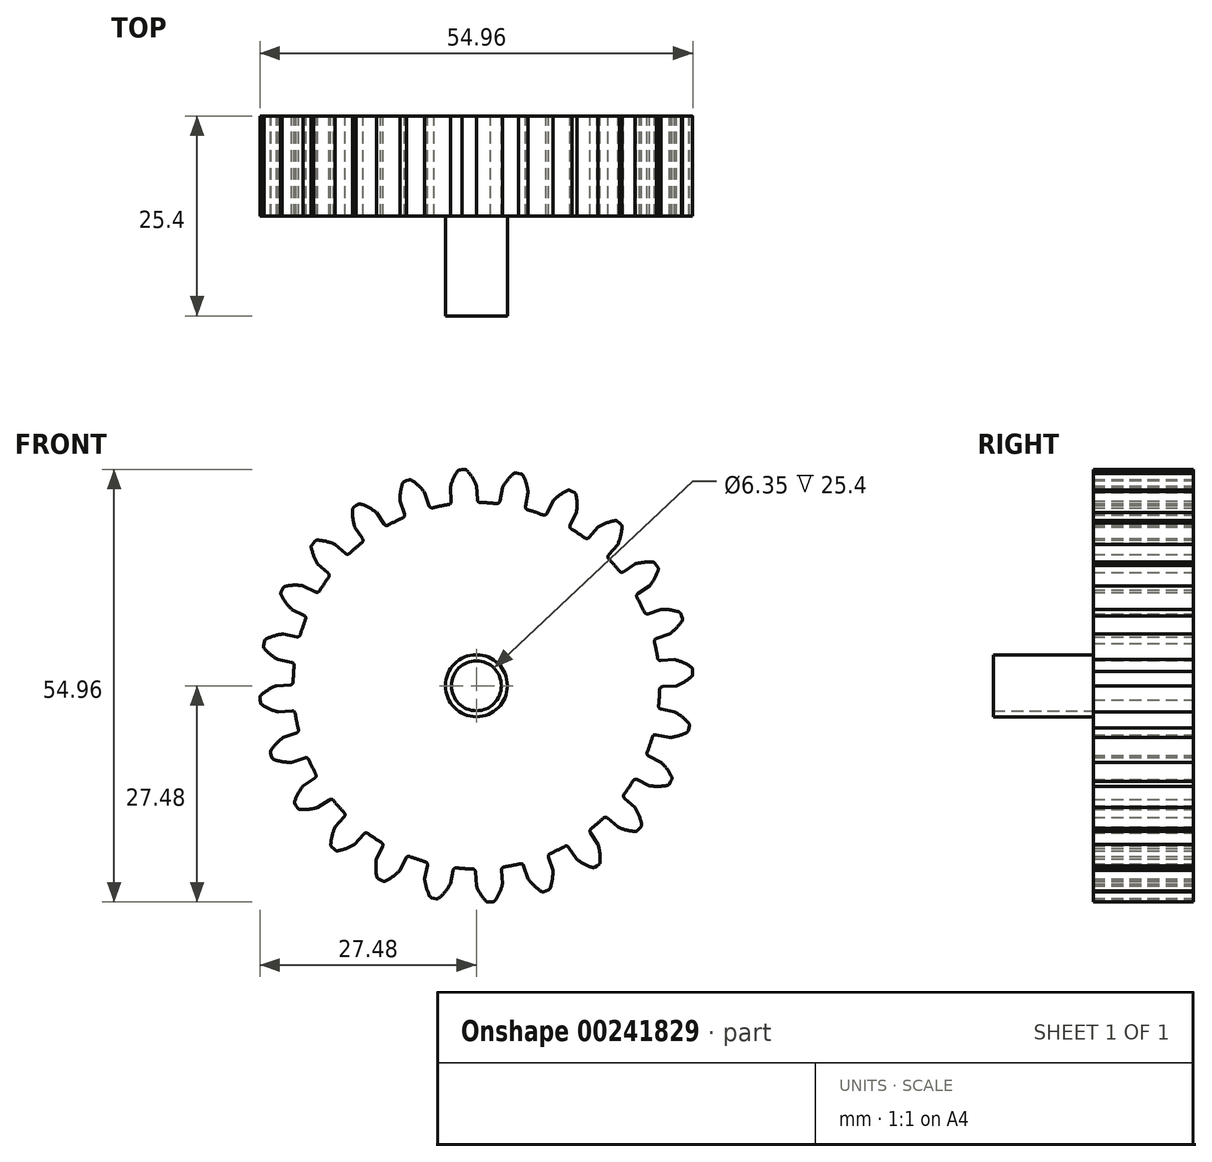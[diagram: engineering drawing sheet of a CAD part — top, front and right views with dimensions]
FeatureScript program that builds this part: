
annotation { "Feature Type Name" : "Feature", "Feature Type Description" : "" }
export const myFeature = defineFeature(function(context is Context, id is Id, definition is map)
    precondition{}
    {
        {
            var Q0;
            Q0=qCreatedBy(makeId("Front.planeOp"),FACE);
            var sketch = newSketch(context, id + "F0", { "sketchPlane" : qUnion([Q0])});
            skArc(sketch, "E0", {"start": v(-3.52, 23.02) * mm, "mid": v(-4.54, 22.84) * mm, "end": v(-5.55, 22.61) * mm});
            skArc(sketch, "E1.trimOffspring", {"start": v(0, 25.4) * mm, "mid": v(-0.5, 26.43) * mm, "end": v(-1.2, 27.35) * mm});
            skLineSegment(sketch, "E2", {"start": v(0, 25.4) * mm, "end": v(0.12, 23.63) * mm});
            skLineSegment(sketch, "E3", {"start": v(-1.5, 27.48) * mm, "end": v(-1.8, 27.46) * mm});
            skLineSegment(sketch, "E4.MirrorCS", {"start": v(-2.1, 27.44) * mm, "end": v(-1.8, 27.46) * mm});
            skArc(sketch, "E5.MirrorCS", {"start": v(-3.32, 25.18) * mm, "mid": v(-2.95, 26.27) * mm, "end": v(-2.39, 27.27) * mm});
            skLineSegment(sketch, "E6.MirrorCS", {"start": v(-3.32, 25.18) * mm, "end": v(-3.2, 23.42) * mm});
            skPoint(sketch, "E7.visualSharp", {"position": v(-2.28, 27.42) * mm});
            skArc(sketch, "E7.filletArc", {"start": v(-2.1, 27.44) * mm, "mid": v(-2.27, 27.39) * mm, "end": v(-2.39, 27.27) * mm});
            skPoint(sketch, "E8.visualSharp", {"position": v(-1.31, 27.49) * mm});
            skArc(sketch, "E8.filletArc", {"start": v(-1.2, 27.35) * mm, "mid": v(-1.33, 27.45) * mm, "end": v(-1.5, 27.48) * mm});
            skPoint(sketch, "E9.visualSharp", {"position": v(0.14, 23.28) * mm});
            skArc(sketch, "E9.filletArc", {"start": v(0.12, 23.63) * mm, "mid": v(0.23, 23.38) * mm, "end": v(0.49, 23.28) * mm});
            skPoint(sketch, "E10.visualSharp", {"position": v(-3.18, 23.07) * mm});
            skArc(sketch, "E10.filletArc", {"start": v(-3.52, 23.02) * mm, "mid": v(-3.28, 23.15) * mm, "end": v(-3.2, 23.42) * mm});
            skPoint(sketch, "E11.1.0", {"position": v(-8.38, 26.2) * mm});
            skPoint(sketch, "E11.1.1", {"position": v(-9.04, 21.46) * mm});
            skArc(sketch, "E11.1.2", {"start": v(-6.57, 24.53) * mm, "mid": v(-7.33, 25.4) * mm, "end": v(-8.23, 26.1) * mm});
            skArc(sketch, "E11.1.3", {"start": v(-9.72, 23.47) * mm, "mid": v(-9.65, 24.61) * mm, "end": v(-9.37, 25.72) * mm});
            skLineSegment(sketch, "E11.1.4", {"start": v(-9.72, 23.47) * mm, "end": v(-9.15, 21.8) * mm});
            skPoint(sketch, "E11.1.5", {"position": v(-9.3, 25.9) * mm});
            skLineSegment(sketch, "E11.1.6", {"start": v(-6.57, 24.53) * mm, "end": v(-6, 22.86) * mm});
            skLineSegment(sketch, "E11.1.7", {"start": v(-9.14, 25.96) * mm, "end": v(-8.85, 26.06) * mm});
            skArc(sketch, "E11.1.8", {"start": v(-9.14, 25.96) * mm, "mid": v(-9.28, 25.87) * mm, "end": v(-9.37, 25.72) * mm});
            skArc(sketch, "E11.1.9", {"start": v(-8.23, 26.1) * mm, "mid": v(-8.39, 26.17) * mm, "end": v(-8.55, 26.15) * mm});
            skLineSegment(sketch, "E11.1.10", {"start": v(-8.55, 26.15) * mm, "end": v(-8.85, 26.06) * mm});
            skArc(sketch, "E11.1.11", {"start": v(-6, 22.86) * mm, "mid": v(-5.83, 22.65) * mm, "end": v(-5.55, 22.61) * mm});
            skArc(sketch, "E11.1.12", {"start": v(-9.36, 21.32) * mm, "mid": v(-9.16, 21.51) * mm, "end": v(-9.15, 21.8) * mm});
            skPoint(sketch, "E11.2.0", {"position": v(-14.88, 23.15) * mm});
            skPoint(sketch, "E11.2.1", {"position": v(-14.28, 18.39) * mm});
            skArc(sketch, "E11.2.2", {"start": v(-12.7, 22) * mm, "mid": v(-13.65, 22.63) * mm, "end": v(-14.7, 23.1) * mm});
            skArc(sketch, "E11.2.3", {"start": v(-15.46, 20.15) * mm, "mid": v(-15.69, 21.28) * mm, "end": v(-15.7, 22.42) * mm});
            skLineSegment(sketch, "E11.2.4", {"start": v(-15.46, 20.15) * mm, "end": v(-14.48, 18.68) * mm});
            skPoint(sketch, "E11.2.5", {"position": v(-15.69, 22.6) * mm});
            skLineSegment(sketch, "E11.2.6", {"start": v(-12.7, 22) * mm, "end": v(-11.72, 20.53) * mm});
            skLineSegment(sketch, "E11.2.7", {"start": v(-15.54, 22.7) * mm, "end": v(-15.29, 22.88) * mm});
            skArc(sketch, "E11.2.8", {"start": v(-15.54, 22.7) * mm, "mid": v(-15.66, 22.58) * mm, "end": v(-15.7, 22.42) * mm});
            skArc(sketch, "E11.2.9", {"start": v(-14.7, 23.1) * mm, "mid": v(-14.87, 23.1) * mm, "end": v(-15.03, 23.05) * mm});
            skLineSegment(sketch, "E11.2.10", {"start": v(-15.03, 23.05) * mm, "end": v(-15.29, 22.88) * mm});
            skArc(sketch, "E11.2.11", {"start": v(-11.72, 20.53) * mm, "mid": v(-11.5, 20.37) * mm, "end": v(-11.22, 20.4) * mm});
            skArc(sketch, "E11.2.12", {"start": v(-14.56, 18.17) * mm, "mid": v(-14.42, 18.41) * mm, "end": v(-14.48, 18.68) * mm});
            skPoint(sketch, "E11.3.0", {"position": v(-20.36, 18.5) * mm});
            skPoint(sketch, "E11.3.1", {"position": v(-18.56, 14.06) * mm});
            skArc(sketch, "E11.3.2", {"start": v(-17.96, 17.96) * mm, "mid": v(-19.05, 18.33) * mm, "end": v(-20.18, 18.5) * mm});
            skArc(sketch, "E11.3.3", {"start": v(-20.15, 15.46) * mm, "mid": v(-20.66, 16.5) * mm, "end": v(-20.97, 17.6) * mm});
            skLineSegment(sketch, "E11.3.4", {"start": v(-20.15, 15.46) * mm, "end": v(-18.82, 14.3) * mm});
            skPoint(sketch, "E11.3.5", {"position": v(-21, 17.77) * mm});
            skLineSegment(sketch, "E11.3.6", {"start": v(-17.96, 17.96) * mm, "end": v(-16.63, 16.8) * mm});
            skLineSegment(sketch, "E11.3.7", {"start": v(-20.9, 17.91) * mm, "end": v(-20.7, 18.15) * mm});
            skArc(sketch, "E11.3.8", {"start": v(-20.9, 17.91) * mm, "mid": v(-20.97, 17.76) * mm, "end": v(-20.97, 17.6) * mm});
            skArc(sketch, "E11.3.9", {"start": v(-20.18, 18.5) * mm, "mid": v(-20.35, 18.47) * mm, "end": v(-20.48, 18.37) * mm});
            skLineSegment(sketch, "E11.3.10", {"start": v(-20.48, 18.37) * mm, "end": v(-20.7, 18.15) * mm});
            skArc(sketch, "E11.3.11", {"start": v(-16.63, 16.8) * mm, "mid": v(-16.37, 16.7) * mm, "end": v(-16.12, 16.8) * mm});
            skArc(sketch, "E11.3.12", {"start": v(-18.76, 13.78) * mm, "mid": v(-18.7, 14.05) * mm, "end": v(-18.82, 14.3) * mm});
            skPoint(sketch, "E11.4.0", {"position": v(-24.46, 12.6) * mm});
            skPoint(sketch, "E11.4.1", {"position": v(-21.56, 8.78) * mm});
            skArc(sketch, "E11.4.2", {"start": v(-22, 12.7) * mm, "mid": v(-23.14, 12.78) * mm, "end": v(-24.28, 12.64) * mm});
            skArc(sketch, "E11.4.3", {"start": v(-23.47, 9.72) * mm, "mid": v(-24.22, 10.58) * mm, "end": v(-24.81, 11.57) * mm});
            skLineSegment(sketch, "E11.4.4", {"start": v(-23.47, 9.72) * mm, "end": v(-21.88, 8.94) * mm});
            skPoint(sketch, "E11.4.5", {"position": v(-24.89, 11.73) * mm});
            skLineSegment(sketch, "E11.4.6", {"start": v(-22, 12.7) * mm, "end": v(-20.4, 11.92) * mm});
            skLineSegment(sketch, "E11.4.7", {"start": v(-24.81, 11.9) * mm, "end": v(-24.68, 12.17) * mm});
            skArc(sketch, "E11.4.8", {"start": v(-24.81, 11.9) * mm, "mid": v(-24.85, 11.73) * mm, "end": v(-24.81, 11.57) * mm});
            skArc(sketch, "E11.4.9", {"start": v(-24.28, 12.64) * mm, "mid": v(-24.43, 12.57) * mm, "end": v(-24.54, 12.45) * mm});
            skLineSegment(sketch, "E11.4.10", {"start": v(-24.54, 12.45) * mm, "end": v(-24.68, 12.17) * mm});
            skArc(sketch, "E11.4.11", {"start": v(-20.4, 11.92) * mm, "mid": v(-20.13, 11.9) * mm, "end": v(-19.92, 12.06) * mm});
            skArc(sketch, "E11.4.12", {"start": v(-21.7, 8.46) * mm, "mid": v(-21.7, 8.73) * mm, "end": v(-21.88, 8.94) * mm});
            skPoint(sketch, "E11.5.0", {"position": v(-26.89, 5.84) * mm});
            skPoint(sketch, "E11.5.1", {"position": v(-23.1, 2.9) * mm});
            skArc(sketch, "E11.5.2", {"start": v(-24.53, 6.57) * mm, "mid": v(-25.66, 6.35) * mm, "end": v(-26.73, 5.93) * mm});
            skArc(sketch, "E11.5.3", {"start": v(-25.18, 3.32) * mm, "mid": v(-26.14, 3.95) * mm, "end": v(-26.96, 4.75) * mm});
            skLineSegment(sketch, "E11.5.4", {"start": v(-25.18, 3.32) * mm, "end": v(-23.45, 2.97) * mm});
            skPoint(sketch, "E11.5.5", {"position": v(-27.08, 4.9) * mm});
            skLineSegment(sketch, "E11.5.6", {"start": v(-24.53, 6.57) * mm, "end": v(-22.8, 6.23) * mm});
            skLineSegment(sketch, "E11.5.7", {"start": v(-27.05, 5.07) * mm, "end": v(-27, 5.37) * mm});
            skArc(sketch, "E11.5.8", {"start": v(-27.05, 5.07) * mm, "mid": v(-27.04, 4.9) * mm, "end": v(-26.96, 4.75) * mm});
            skArc(sketch, "E11.5.9", {"start": v(-26.73, 5.93) * mm, "mid": v(-26.86, 5.82) * mm, "end": v(-26.93, 5.67) * mm});
            skLineSegment(sketch, "E11.5.10", {"start": v(-26.93, 5.67) * mm, "end": v(-27, 5.37) * mm});
            skArc(sketch, "E11.5.11", {"start": v(-22.8, 6.23) * mm, "mid": v(-22.53, 6.28) * mm, "end": v(-22.36, 6.5) * mm});
            skArc(sketch, "E11.5.12", {"start": v(-23.14, 2.55) * mm, "mid": v(-23.21, 2.82) * mm, "end": v(-23.45, 2.97) * mm});
            skPoint(sketch, "E11.6.0", {"position": v(-27.49, -1.31) * mm});
            skPoint(sketch, "E11.6.1", {"position": v(-23.07, -3.18) * mm});
            skArc(sketch, "E11.6.2", {"start": v(-25.4, 0) * mm, "mid": v(-26.43, -0.5) * mm, "end": v(-27.35, -1.2) * mm});
            skArc(sketch, "E11.6.3", {"start": v(-25.18, -3.32) * mm, "mid": v(-26.27, -2.95) * mm, "end": v(-27.27, -2.39) * mm});
            skLineSegment(sketch, "E11.6.4", {"start": v(-25.18, -3.32) * mm, "end": v(-23.42, -3.2) * mm});
            skPoint(sketch, "E11.6.5", {"position": v(-27.42, -2.28) * mm});
            skLineSegment(sketch, "E11.6.6", {"start": v(-25.4, 0) * mm, "end": v(-23.63, 0.12) * mm});
            skLineSegment(sketch, "E11.6.7", {"start": v(-27.44, -2.1) * mm, "end": v(-27.46, -1.8) * mm});
            skArc(sketch, "E11.6.8", {"start": v(-27.44, -2.1) * mm, "mid": v(-27.39, -2.27) * mm, "end": v(-27.27, -2.39) * mm});
            skArc(sketch, "E11.6.9", {"start": v(-27.35, -1.2) * mm, "mid": v(-27.45, -1.33) * mm, "end": v(-27.48, -1.5) * mm});
            skLineSegment(sketch, "E11.6.10", {"start": v(-27.48, -1.5) * mm, "end": v(-27.46, -1.8) * mm});
            skArc(sketch, "E11.6.11", {"start": v(-23.63, 0.12) * mm, "mid": v(-23.38, 0.23) * mm, "end": v(-23.28, 0.49) * mm});
            skArc(sketch, "E11.6.12", {"start": v(-23.02, -3.52) * mm, "mid": v(-23.15, -3.28) * mm, "end": v(-23.42, -3.2) * mm});
            skPoint(sketch, "E11.7.0", {"position": v(-26.2, -8.38) * mm});
            skPoint(sketch, "E11.7.1", {"position": v(-21.46, -9.04) * mm});
            skArc(sketch, "E11.7.2", {"start": v(-24.53, -6.57) * mm, "mid": v(-25.4, -7.33) * mm, "end": v(-26.1, -8.23) * mm});
            skArc(sketch, "E11.7.3", {"start": v(-23.47, -9.72) * mm, "mid": v(-24.61, -9.65) * mm, "end": v(-25.72, -9.37) * mm});
            skLineSegment(sketch, "E11.7.4", {"start": v(-23.47, -9.72) * mm, "end": v(-21.8, -9.15) * mm});
            skPoint(sketch, "E11.7.5", {"position": v(-25.9, -9.3) * mm});
            skLineSegment(sketch, "E11.7.6", {"start": v(-24.53, -6.57) * mm, "end": v(-22.86, -6) * mm});
            skLineSegment(sketch, "E11.7.7", {"start": v(-25.96, -9.14) * mm, "end": v(-26.06, -8.85) * mm});
            skArc(sketch, "E11.7.8", {"start": v(-25.96, -9.14) * mm, "mid": v(-25.87, -9.28) * mm, "end": v(-25.72, -9.37) * mm});
            skArc(sketch, "E11.7.9", {"start": v(-26.1, -8.23) * mm, "mid": v(-26.17, -8.39) * mm, "end": v(-26.15, -8.55) * mm});
            skLineSegment(sketch, "E11.7.10", {"start": v(-26.15, -8.55) * mm, "end": v(-26.06, -8.85) * mm});
            skArc(sketch, "E11.7.11", {"start": v(-22.86, -6) * mm, "mid": v(-22.65, -5.83) * mm, "end": v(-22.61, -5.55) * mm});
            skArc(sketch, "E11.7.12", {"start": v(-21.32, -9.36) * mm, "mid": v(-21.51, -9.16) * mm, "end": v(-21.8, -9.15) * mm});
            skPoint(sketch, "E11.8.0", {"position": v(-23.15, -14.88) * mm});
            skPoint(sketch, "E11.8.1", {"position": v(-18.39, -14.28) * mm});
            skArc(sketch, "E11.8.2", {"start": v(-22, -12.7) * mm, "mid": v(-22.63, -13.65) * mm, "end": v(-23.1, -14.7) * mm});
            skArc(sketch, "E11.8.3", {"start": v(-20.15, -15.46) * mm, "mid": v(-21.28, -15.69) * mm, "end": v(-22.42, -15.7) * mm});
            skLineSegment(sketch, "E11.8.4", {"start": v(-20.15, -15.46) * mm, "end": v(-18.68, -14.48) * mm});
            skPoint(sketch, "E11.8.5", {"position": v(-22.6, -15.69) * mm});
            skLineSegment(sketch, "E11.8.6", {"start": v(-22, -12.7) * mm, "end": v(-20.53, -11.72) * mm});
            skLineSegment(sketch, "E11.8.7", {"start": v(-22.7, -15.54) * mm, "end": v(-22.88, -15.29) * mm});
            skArc(sketch, "E11.8.8", {"start": v(-22.7, -15.54) * mm, "mid": v(-22.58, -15.66) * mm, "end": v(-22.42, -15.7) * mm});
            skArc(sketch, "E11.8.9", {"start": v(-23.1, -14.7) * mm, "mid": v(-23.1, -14.87) * mm, "end": v(-23.05, -15.03) * mm});
            skLineSegment(sketch, "E11.8.10", {"start": v(-23.05, -15.03) * mm, "end": v(-22.88, -15.29) * mm});
            skArc(sketch, "E11.8.11", {"start": v(-20.53, -11.72) * mm, "mid": v(-20.37, -11.5) * mm, "end": v(-20.4, -11.22) * mm});
            skArc(sketch, "E11.8.12", {"start": v(-18.17, -14.56) * mm, "mid": v(-18.41, -14.42) * mm, "end": v(-18.68, -14.48) * mm});
            skPoint(sketch, "E11.9.0", {"position": v(-18.5, -20.36) * mm});
            skPoint(sketch, "E11.9.1", {"position": v(-14.06, -18.56) * mm});
            skArc(sketch, "E11.9.2", {"start": v(-17.96, -17.96) * mm, "mid": v(-18.33, -19.05) * mm, "end": v(-18.5, -20.18) * mm});
            skArc(sketch, "E11.9.3", {"start": v(-15.46, -20.15) * mm, "mid": v(-16.5, -20.66) * mm, "end": v(-17.6, -20.97) * mm});
            skLineSegment(sketch, "E11.9.4", {"start": v(-15.46, -20.15) * mm, "end": v(-14.3, -18.82) * mm});
            skPoint(sketch, "E11.9.5", {"position": v(-17.77, -21) * mm});
            skLineSegment(sketch, "E11.9.6", {"start": v(-17.96, -17.96) * mm, "end": v(-16.8, -16.63) * mm});
            skLineSegment(sketch, "E11.9.7", {"start": v(-17.91, -20.9) * mm, "end": v(-18.15, -20.7) * mm});
            skArc(sketch, "E11.9.8", {"start": v(-17.91, -20.9) * mm, "mid": v(-17.76, -20.97) * mm, "end": v(-17.6, -20.97) * mm});
            skArc(sketch, "E11.9.9", {"start": v(-18.5, -20.18) * mm, "mid": v(-18.47, -20.35) * mm, "end": v(-18.37, -20.48) * mm});
            skLineSegment(sketch, "E11.9.10", {"start": v(-18.37, -20.48) * mm, "end": v(-18.15, -20.7) * mm});
            skArc(sketch, "E11.9.11", {"start": v(-16.8, -16.63) * mm, "mid": v(-16.7, -16.37) * mm, "end": v(-16.8, -16.12) * mm});
            skArc(sketch, "E11.9.12", {"start": v(-13.78, -18.76) * mm, "mid": v(-14.05, -18.7) * mm, "end": v(-14.3, -18.82) * mm});
            skPoint(sketch, "E11.10.0", {"position": v(-12.6, -24.46) * mm});
            skPoint(sketch, "E11.10.1", {"position": v(-8.78, -21.56) * mm});
            skArc(sketch, "E11.10.2", {"start": v(-12.7, -22) * mm, "mid": v(-12.78, -23.14) * mm, "end": v(-12.64, -24.28) * mm});
            skArc(sketch, "E11.10.3", {"start": v(-9.72, -23.47) * mm, "mid": v(-10.58, -24.22) * mm, "end": v(-11.57, -24.81) * mm});
            skLineSegment(sketch, "E11.10.4", {"start": v(-9.72, -23.47) * mm, "end": v(-8.94, -21.88) * mm});
            skPoint(sketch, "E11.10.5", {"position": v(-11.73, -24.89) * mm});
            skLineSegment(sketch, "E11.10.6", {"start": v(-12.7, -22) * mm, "end": v(-11.92, -20.4) * mm});
            skLineSegment(sketch, "E11.10.7", {"start": v(-11.9, -24.81) * mm, "end": v(-12.17, -24.68) * mm});
            skArc(sketch, "E11.10.8", {"start": v(-11.9, -24.81) * mm, "mid": v(-11.73, -24.85) * mm, "end": v(-11.57, -24.81) * mm});
            skArc(sketch, "E11.10.9", {"start": v(-12.64, -24.28) * mm, "mid": v(-12.57, -24.43) * mm, "end": v(-12.45, -24.54) * mm});
            skLineSegment(sketch, "E11.10.10", {"start": v(-12.45, -24.54) * mm, "end": v(-12.17, -24.68) * mm});
            skArc(sketch, "E11.10.11", {"start": v(-11.92, -20.4) * mm, "mid": v(-11.9, -20.13) * mm, "end": v(-12.06, -19.92) * mm});
            skArc(sketch, "E11.10.12", {"start": v(-8.46, -21.7) * mm, "mid": v(-8.73, -21.7) * mm, "end": v(-8.94, -21.88) * mm});
            skPoint(sketch, "E11.11.0", {"position": v(-5.84, -26.89) * mm});
            skPoint(sketch, "E11.11.1", {"position": v(-2.9, -23.1) * mm});
            skArc(sketch, "E11.11.2", {"start": v(-6.57, -24.53) * mm, "mid": v(-6.35, -25.66) * mm, "end": v(-5.93, -26.73) * mm});
            skArc(sketch, "E11.11.3", {"start": v(-3.32, -25.18) * mm, "mid": v(-3.95, -26.14) * mm, "end": v(-4.75, -26.96) * mm});
            skLineSegment(sketch, "E11.11.4", {"start": v(-3.32, -25.18) * mm, "end": v(-2.97, -23.45) * mm});
            skPoint(sketch, "E11.11.5", {"position": v(-4.9, -27.08) * mm});
            skLineSegment(sketch, "E11.11.6", {"start": v(-6.57, -24.53) * mm, "end": v(-6.23, -22.8) * mm});
            skLineSegment(sketch, "E11.11.7", {"start": v(-5.07, -27.05) * mm, "end": v(-5.37, -27) * mm});
            skArc(sketch, "E11.11.8", {"start": v(-5.07, -27.05) * mm, "mid": v(-4.9, -27.04) * mm, "end": v(-4.75, -26.96) * mm});
            skArc(sketch, "E11.11.9", {"start": v(-5.93, -26.73) * mm, "mid": v(-5.82, -26.86) * mm, "end": v(-5.67, -26.93) * mm});
            skLineSegment(sketch, "E11.11.10", {"start": v(-5.67, -26.93) * mm, "end": v(-5.37, -27) * mm});
            skArc(sketch, "E11.11.11", {"start": v(-6.23, -22.8) * mm, "mid": v(-6.28, -22.53) * mm, "end": v(-6.5, -22.36) * mm});
            skArc(sketch, "E11.11.12", {"start": v(-2.55, -23.14) * mm, "mid": v(-2.82, -23.21) * mm, "end": v(-2.97, -23.45) * mm});
            skPoint(sketch, "E11.12.0", {"position": v(1.31, -27.49) * mm});
            skPoint(sketch, "E11.12.1", {"position": v(3.18, -23.07) * mm});
            skArc(sketch, "E11.12.2", {"start": v(0, -25.4) * mm, "mid": v(0.5, -26.43) * mm, "end": v(1.2, -27.35) * mm});
            skArc(sketch, "E11.12.3", {"start": v(3.32, -25.18) * mm, "mid": v(2.95, -26.27) * mm, "end": v(2.39, -27.27) * mm});
            skLineSegment(sketch, "E11.12.4", {"start": v(3.32, -25.18) * mm, "end": v(3.2, -23.42) * mm});
            skPoint(sketch, "E11.12.5", {"position": v(2.28, -27.42) * mm});
            skLineSegment(sketch, "E11.12.6", {"start": v(0, -25.4) * mm, "end": v(-0.12, -23.63) * mm});
            skLineSegment(sketch, "E11.12.7", {"start": v(2.1, -27.44) * mm, "end": v(1.8, -27.46) * mm});
            skArc(sketch, "E11.12.8", {"start": v(2.1, -27.44) * mm, "mid": v(2.27, -27.39) * mm, "end": v(2.39, -27.27) * mm});
            skArc(sketch, "E11.12.9", {"start": v(1.2, -27.35) * mm, "mid": v(1.33, -27.45) * mm, "end": v(1.5, -27.48) * mm});
            skLineSegment(sketch, "E11.12.10", {"start": v(1.5, -27.48) * mm, "end": v(1.8, -27.46) * mm});
            skArc(sketch, "E11.12.11", {"start": v(-0.12, -23.63) * mm, "mid": v(-0.23, -23.38) * mm, "end": v(-0.49, -23.28) * mm});
            skArc(sketch, "E11.12.12", {"start": v(3.52, -23.02) * mm, "mid": v(3.28, -23.15) * mm, "end": v(3.2, -23.42) * mm});
            skPoint(sketch, "E11.13.0", {"position": v(8.38, -26.2) * mm});
            skPoint(sketch, "E11.13.1", {"position": v(9.04, -21.46) * mm});
            skArc(sketch, "E11.13.2", {"start": v(6.57, -24.53) * mm, "mid": v(7.33, -25.4) * mm, "end": v(8.23, -26.1) * mm});
            skArc(sketch, "E11.13.3", {"start": v(9.72, -23.47) * mm, "mid": v(9.65, -24.61) * mm, "end": v(9.37, -25.72) * mm});
            skLineSegment(sketch, "E11.13.4", {"start": v(9.72, -23.47) * mm, "end": v(9.15, -21.8) * mm});
            skPoint(sketch, "E11.13.5", {"position": v(9.3, -25.9) * mm});
            skLineSegment(sketch, "E11.13.6", {"start": v(6.57, -24.53) * mm, "end": v(6, -22.86) * mm});
            skLineSegment(sketch, "E11.13.7", {"start": v(9.14, -25.96) * mm, "end": v(8.85, -26.06) * mm});
            skArc(sketch, "E11.13.8", {"start": v(9.14, -25.96) * mm, "mid": v(9.28, -25.87) * mm, "end": v(9.37, -25.72) * mm});
            skArc(sketch, "E11.13.9", {"start": v(8.23, -26.1) * mm, "mid": v(8.39, -26.17) * mm, "end": v(8.55, -26.15) * mm});
            skLineSegment(sketch, "E11.13.10", {"start": v(8.55, -26.15) * mm, "end": v(8.85, -26.06) * mm});
            skArc(sketch, "E11.13.11", {"start": v(6, -22.86) * mm, "mid": v(5.83, -22.65) * mm, "end": v(5.55, -22.61) * mm});
            skArc(sketch, "E11.13.12", {"start": v(9.36, -21.32) * mm, "mid": v(9.16, -21.51) * mm, "end": v(9.15, -21.8) * mm});
            skPoint(sketch, "E11.14.0", {"position": v(14.88, -23.15) * mm});
            skPoint(sketch, "E11.14.1", {"position": v(14.28, -18.39) * mm});
            skArc(sketch, "E11.14.2", {"start": v(12.7, -22) * mm, "mid": v(13.65, -22.63) * mm, "end": v(14.7, -23.1) * mm});
            skArc(sketch, "E11.14.3", {"start": v(15.46, -20.15) * mm, "mid": v(15.69, -21.28) * mm, "end": v(15.7, -22.42) * mm});
            skLineSegment(sketch, "E11.14.4", {"start": v(15.46, -20.15) * mm, "end": v(14.48, -18.68) * mm});
            skPoint(sketch, "E11.14.5", {"position": v(15.69, -22.6) * mm});
            skLineSegment(sketch, "E11.14.6", {"start": v(12.7, -22) * mm, "end": v(11.72, -20.53) * mm});
            skLineSegment(sketch, "E11.14.7", {"start": v(15.54, -22.7) * mm, "end": v(15.29, -22.88) * mm});
            skArc(sketch, "E11.14.8", {"start": v(15.54, -22.7) * mm, "mid": v(15.66, -22.58) * mm, "end": v(15.7, -22.42) * mm});
            skArc(sketch, "E11.14.9", {"start": v(14.7, -23.1) * mm, "mid": v(14.87, -23.1) * mm, "end": v(15.03, -23.05) * mm});
            skLineSegment(sketch, "E11.14.10", {"start": v(15.03, -23.05) * mm, "end": v(15.29, -22.88) * mm});
            skArc(sketch, "E11.14.11", {"start": v(11.72, -20.53) * mm, "mid": v(11.5, -20.37) * mm, "end": v(11.22, -20.4) * mm});
            skArc(sketch, "E11.14.12", {"start": v(14.56, -18.17) * mm, "mid": v(14.42, -18.41) * mm, "end": v(14.48, -18.68) * mm});
            skPoint(sketch, "E11.15.0", {"position": v(20.36, -18.5) * mm});
            skPoint(sketch, "E11.15.1", {"position": v(18.56, -14.06) * mm});
            skArc(sketch, "E11.15.2", {"start": v(17.96, -17.96) * mm, "mid": v(19.05, -18.33) * mm, "end": v(20.18, -18.5) * mm});
            skArc(sketch, "E11.15.3", {"start": v(20.15, -15.46) * mm, "mid": v(20.66, -16.5) * mm, "end": v(20.97, -17.6) * mm});
            skLineSegment(sketch, "E11.15.4", {"start": v(20.15, -15.46) * mm, "end": v(18.82, -14.3) * mm});
            skPoint(sketch, "E11.15.5", {"position": v(21, -17.77) * mm});
            skLineSegment(sketch, "E11.15.6", {"start": v(17.96, -17.96) * mm, "end": v(16.63, -16.8) * mm});
            skLineSegment(sketch, "E11.15.7", {"start": v(20.9, -17.91) * mm, "end": v(20.7, -18.15) * mm});
            skArc(sketch, "E11.15.8", {"start": v(20.9, -17.91) * mm, "mid": v(20.97, -17.76) * mm, "end": v(20.97, -17.6) * mm});
            skArc(sketch, "E11.15.9", {"start": v(20.18, -18.5) * mm, "mid": v(20.35, -18.47) * mm, "end": v(20.48, -18.37) * mm});
            skLineSegment(sketch, "E11.15.10", {"start": v(20.48, -18.37) * mm, "end": v(20.7, -18.15) * mm});
            skArc(sketch, "E11.15.11", {"start": v(16.63, -16.8) * mm, "mid": v(16.37, -16.7) * mm, "end": v(16.12, -16.8) * mm});
            skArc(sketch, "E11.15.12", {"start": v(18.76, -13.78) * mm, "mid": v(18.7, -14.05) * mm, "end": v(18.82, -14.3) * mm});
            skPoint(sketch, "E11.16.0", {"position": v(24.46, -12.6) * mm});
            skPoint(sketch, "E11.16.1", {"position": v(21.56, -8.78) * mm});
            skArc(sketch, "E11.16.2", {"start": v(22, -12.7) * mm, "mid": v(23.14, -12.78) * mm, "end": v(24.28, -12.64) * mm});
            skArc(sketch, "E11.16.3", {"start": v(23.47, -9.72) * mm, "mid": v(24.22, -10.58) * mm, "end": v(24.81, -11.57) * mm});
            skLineSegment(sketch, "E11.16.4", {"start": v(23.47, -9.72) * mm, "end": v(21.88, -8.94) * mm});
            skPoint(sketch, "E11.16.5", {"position": v(24.89, -11.73) * mm});
            skLineSegment(sketch, "E11.16.6", {"start": v(22, -12.7) * mm, "end": v(20.4, -11.92) * mm});
            skLineSegment(sketch, "E11.16.7", {"start": v(24.81, -11.9) * mm, "end": v(24.68, -12.17) * mm});
            skArc(sketch, "E11.16.8", {"start": v(24.81, -11.9) * mm, "mid": v(24.85, -11.73) * mm, "end": v(24.81, -11.57) * mm});
            skArc(sketch, "E11.16.9", {"start": v(24.28, -12.64) * mm, "mid": v(24.43, -12.57) * mm, "end": v(24.54, -12.45) * mm});
            skLineSegment(sketch, "E11.16.10", {"start": v(24.54, -12.45) * mm, "end": v(24.68, -12.17) * mm});
            skArc(sketch, "E11.16.11", {"start": v(20.4, -11.92) * mm, "mid": v(20.13, -11.9) * mm, "end": v(19.92, -12.06) * mm});
            skArc(sketch, "E11.16.12", {"start": v(21.7, -8.46) * mm, "mid": v(21.7, -8.73) * mm, "end": v(21.88, -8.94) * mm});
            skPoint(sketch, "E11.17.0", {"position": v(26.89, -5.84) * mm});
            skPoint(sketch, "E11.17.1", {"position": v(23.1, -2.9) * mm});
            skArc(sketch, "E11.17.2", {"start": v(24.53, -6.57) * mm, "mid": v(25.66, -6.35) * mm, "end": v(26.73, -5.93) * mm});
            skArc(sketch, "E11.17.3", {"start": v(25.18, -3.32) * mm, "mid": v(26.14, -3.95) * mm, "end": v(26.96, -4.75) * mm});
            skLineSegment(sketch, "E11.17.4", {"start": v(25.18, -3.32) * mm, "end": v(23.45, -2.97) * mm});
            skPoint(sketch, "E11.17.5", {"position": v(27.08, -4.9) * mm});
            skLineSegment(sketch, "E11.17.6", {"start": v(24.53, -6.57) * mm, "end": v(22.8, -6.23) * mm});
            skLineSegment(sketch, "E11.17.7", {"start": v(27.05, -5.07) * mm, "end": v(27, -5.37) * mm});
            skArc(sketch, "E11.17.8", {"start": v(27.05, -5.07) * mm, "mid": v(27.04, -4.9) * mm, "end": v(26.96, -4.75) * mm});
            skArc(sketch, "E11.17.9", {"start": v(26.73, -5.93) * mm, "mid": v(26.86, -5.82) * mm, "end": v(26.93, -5.67) * mm});
            skLineSegment(sketch, "E11.17.10", {"start": v(26.93, -5.67) * mm, "end": v(27, -5.37) * mm});
            skArc(sketch, "E11.17.11", {"start": v(22.8, -6.23) * mm, "mid": v(22.53, -6.28) * mm, "end": v(22.36, -6.5) * mm});
            skArc(sketch, "E11.17.12", {"start": v(23.14, -2.55) * mm, "mid": v(23.21, -2.82) * mm, "end": v(23.45, -2.97) * mm});
            skPoint(sketch, "E11.18.0", {"position": v(27.49, 1.31) * mm});
            skPoint(sketch, "E11.18.1", {"position": v(23.07, 3.18) * mm});
            skArc(sketch, "E11.18.2", {"start": v(25.4, 0) * mm, "mid": v(26.43, 0.5) * mm, "end": v(27.35, 1.2) * mm});
            skArc(sketch, "E11.18.3", {"start": v(25.18, 3.32) * mm, "mid": v(26.27, 2.95) * mm, "end": v(27.27, 2.39) * mm});
            skLineSegment(sketch, "E11.18.4", {"start": v(25.18, 3.32) * mm, "end": v(23.42, 3.2) * mm});
            skPoint(sketch, "E11.18.5", {"position": v(27.42, 2.28) * mm});
            skLineSegment(sketch, "E11.18.6", {"start": v(25.4, 0) * mm, "end": v(23.63, -0.12) * mm});
            skLineSegment(sketch, "E11.18.7", {"start": v(27.44, 2.1) * mm, "end": v(27.46, 1.8) * mm});
            skArc(sketch, "E11.18.8", {"start": v(27.44, 2.1) * mm, "mid": v(27.39, 2.27) * mm, "end": v(27.27, 2.39) * mm});
            skArc(sketch, "E11.18.9", {"start": v(27.35, 1.2) * mm, "mid": v(27.45, 1.33) * mm, "end": v(27.48, 1.5) * mm});
            skLineSegment(sketch, "E11.18.10", {"start": v(27.48, 1.5) * mm, "end": v(27.46, 1.8) * mm});
            skArc(sketch, "E11.18.11", {"start": v(23.63, -0.12) * mm, "mid": v(23.38, -0.23) * mm, "end": v(23.28, -0.49) * mm});
            skArc(sketch, "E11.18.12", {"start": v(23.02, 3.52) * mm, "mid": v(23.15, 3.28) * mm, "end": v(23.42, 3.2) * mm});
            skPoint(sketch, "E11.19.0", {"position": v(26.2, 8.38) * mm});
            skPoint(sketch, "E11.19.1", {"position": v(21.46, 9.04) * mm});
            skArc(sketch, "E11.19.2", {"start": v(24.53, 6.57) * mm, "mid": v(25.4, 7.33) * mm, "end": v(26.1, 8.23) * mm});
            skArc(sketch, "E11.19.3", {"start": v(23.47, 9.72) * mm, "mid": v(24.61, 9.65) * mm, "end": v(25.72, 9.37) * mm});
            skLineSegment(sketch, "E11.19.4", {"start": v(23.47, 9.72) * mm, "end": v(21.8, 9.15) * mm});
            skPoint(sketch, "E11.19.5", {"position": v(25.9, 9.3) * mm});
            skLineSegment(sketch, "E11.19.6", {"start": v(24.53, 6.57) * mm, "end": v(22.86, 6) * mm});
            skLineSegment(sketch, "E11.19.7", {"start": v(25.96, 9.14) * mm, "end": v(26.06, 8.85) * mm});
            skArc(sketch, "E11.19.8", {"start": v(25.96, 9.14) * mm, "mid": v(25.87, 9.28) * mm, "end": v(25.72, 9.37) * mm});
            skArc(sketch, "E11.19.9", {"start": v(26.1, 8.23) * mm, "mid": v(26.17, 8.39) * mm, "end": v(26.15, 8.55) * mm});
            skLineSegment(sketch, "E11.19.10", {"start": v(26.15, 8.55) * mm, "end": v(26.06, 8.85) * mm});
            skArc(sketch, "E11.19.11", {"start": v(22.86, 6) * mm, "mid": v(22.65, 5.83) * mm, "end": v(22.61, 5.55) * mm});
            skArc(sketch, "E11.19.12", {"start": v(21.32, 9.36) * mm, "mid": v(21.51, 9.16) * mm, "end": v(21.8, 9.15) * mm});
            skPoint(sketch, "E11.20.0", {"position": v(23.15, 14.88) * mm});
            skPoint(sketch, "E11.20.1", {"position": v(18.39, 14.28) * mm});
            skArc(sketch, "E11.20.2", {"start": v(22, 12.7) * mm, "mid": v(22.63, 13.65) * mm, "end": v(23.1, 14.7) * mm});
            skArc(sketch, "E11.20.3", {"start": v(20.15, 15.46) * mm, "mid": v(21.28, 15.69) * mm, "end": v(22.42, 15.7) * mm});
            skLineSegment(sketch, "E11.20.4", {"start": v(20.15, 15.46) * mm, "end": v(18.68, 14.48) * mm});
            skPoint(sketch, "E11.20.5", {"position": v(22.6, 15.69) * mm});
            skLineSegment(sketch, "E11.20.6", {"start": v(22, 12.7) * mm, "end": v(20.53, 11.72) * mm});
            skLineSegment(sketch, "E11.20.7", {"start": v(22.7, 15.54) * mm, "end": v(22.88, 15.29) * mm});
            skArc(sketch, "E11.20.8", {"start": v(22.7, 15.54) * mm, "mid": v(22.58, 15.66) * mm, "end": v(22.42, 15.7) * mm});
            skArc(sketch, "E11.20.9", {"start": v(23.1, 14.7) * mm, "mid": v(23.1, 14.87) * mm, "end": v(23.05, 15.03) * mm});
            skLineSegment(sketch, "E11.20.10", {"start": v(23.05, 15.03) * mm, "end": v(22.88, 15.29) * mm});
            skArc(sketch, "E11.20.11", {"start": v(20.53, 11.72) * mm, "mid": v(20.37, 11.5) * mm, "end": v(20.4, 11.22) * mm});
            skArc(sketch, "E11.20.12", {"start": v(18.17, 14.56) * mm, "mid": v(18.41, 14.42) * mm, "end": v(18.68, 14.48) * mm});
            skPoint(sketch, "E11.21.0", {"position": v(18.5, 20.36) * mm});
            skPoint(sketch, "E11.21.1", {"position": v(14.06, 18.56) * mm});
            skArc(sketch, "E11.21.2", {"start": v(17.96, 17.96) * mm, "mid": v(18.33, 19.05) * mm, "end": v(18.5, 20.18) * mm});
            skArc(sketch, "E11.21.3", {"start": v(15.46, 20.15) * mm, "mid": v(16.5, 20.66) * mm, "end": v(17.6, 20.97) * mm});
            skLineSegment(sketch, "E11.21.4", {"start": v(15.46, 20.15) * mm, "end": v(14.3, 18.82) * mm});
            skPoint(sketch, "E11.21.5", {"position": v(17.77, 21) * mm});
            skLineSegment(sketch, "E11.21.6", {"start": v(17.96, 17.96) * mm, "end": v(16.8, 16.63) * mm});
            skLineSegment(sketch, "E11.21.7", {"start": v(17.91, 20.9) * mm, "end": v(18.15, 20.7) * mm});
            skArc(sketch, "E11.21.8", {"start": v(17.91, 20.9) * mm, "mid": v(17.76, 20.97) * mm, "end": v(17.6, 20.97) * mm});
            skArc(sketch, "E11.21.9", {"start": v(18.5, 20.18) * mm, "mid": v(18.47, 20.35) * mm, "end": v(18.37, 20.48) * mm});
            skLineSegment(sketch, "E11.21.10", {"start": v(18.37, 20.48) * mm, "end": v(18.15, 20.7) * mm});
            skArc(sketch, "E11.21.11", {"start": v(16.8, 16.63) * mm, "mid": v(16.7, 16.37) * mm, "end": v(16.8, 16.12) * mm});
            skArc(sketch, "E11.21.12", {"start": v(13.78, 18.76) * mm, "mid": v(14.05, 18.7) * mm, "end": v(14.3, 18.82) * mm});
            skPoint(sketch, "E11.22.0", {"position": v(12.6, 24.46) * mm});
            skPoint(sketch, "E11.22.1", {"position": v(8.78, 21.56) * mm});
            skArc(sketch, "E11.22.2", {"start": v(12.7, 22) * mm, "mid": v(12.78, 23.14) * mm, "end": v(12.64, 24.28) * mm});
            skArc(sketch, "E11.22.3", {"start": v(9.72, 23.47) * mm, "mid": v(10.58, 24.22) * mm, "end": v(11.57, 24.81) * mm});
            skLineSegment(sketch, "E11.22.4", {"start": v(9.72, 23.47) * mm, "end": v(8.94, 21.88) * mm});
            skPoint(sketch, "E11.22.5", {"position": v(11.73, 24.89) * mm});
            skLineSegment(sketch, "E11.22.6", {"start": v(12.7, 22) * mm, "end": v(11.92, 20.4) * mm});
            skLineSegment(sketch, "E11.22.7", {"start": v(11.9, 24.81) * mm, "end": v(12.17, 24.68) * mm});
            skArc(sketch, "E11.22.8", {"start": v(11.9, 24.81) * mm, "mid": v(11.73, 24.85) * mm, "end": v(11.57, 24.81) * mm});
            skArc(sketch, "E11.22.9", {"start": v(12.64, 24.28) * mm, "mid": v(12.57, 24.43) * mm, "end": v(12.45, 24.54) * mm});
            skLineSegment(sketch, "E11.22.10", {"start": v(12.45, 24.54) * mm, "end": v(12.17, 24.68) * mm});
            skArc(sketch, "E11.22.11", {"start": v(11.92, 20.4) * mm, "mid": v(11.9, 20.13) * mm, "end": v(12.06, 19.92) * mm});
            skArc(sketch, "E11.22.12", {"start": v(8.46, 21.7) * mm, "mid": v(8.73, 21.7) * mm, "end": v(8.94, 21.88) * mm});
            skPoint(sketch, "E11.23.0", {"position": v(5.84, 26.89) * mm});
            skPoint(sketch, "E11.23.1", {"position": v(2.9, 23.1) * mm});
            skArc(sketch, "E11.23.2", {"start": v(6.57, 24.53) * mm, "mid": v(6.35, 25.66) * mm, "end": v(5.93, 26.73) * mm});
            skArc(sketch, "E11.23.3", {"start": v(3.32, 25.18) * mm, "mid": v(3.95, 26.14) * mm, "end": v(4.75, 26.96) * mm});
            skLineSegment(sketch, "E11.23.4", {"start": v(3.32, 25.18) * mm, "end": v(2.97, 23.45) * mm});
            skPoint(sketch, "E11.23.5", {"position": v(4.9, 27.08) * mm});
            skLineSegment(sketch, "E11.23.6", {"start": v(6.57, 24.53) * mm, "end": v(6.23, 22.8) * mm});
            skLineSegment(sketch, "E11.23.7", {"start": v(5.07, 27.05) * mm, "end": v(5.37, 27) * mm});
            skArc(sketch, "E11.23.8", {"start": v(5.07, 27.05) * mm, "mid": v(4.9, 27.04) * mm, "end": v(4.75, 26.96) * mm});
            skArc(sketch, "E11.23.9", {"start": v(5.93, 26.73) * mm, "mid": v(5.82, 26.86) * mm, "end": v(5.67, 26.93) * mm});
            skLineSegment(sketch, "E11.23.10", {"start": v(5.67, 26.93) * mm, "end": v(5.37, 27) * mm});
            skArc(sketch, "E11.23.11", {"start": v(6.23, 22.8) * mm, "mid": v(6.28, 22.53) * mm, "end": v(6.5, 22.36) * mm});
            skArc(sketch, "E11.23.12", {"start": v(2.55, 23.14) * mm, "mid": v(2.82, 23.21) * mm, "end": v(2.97, 23.45) * mm});
            skArc(sketch, "E12.trimOffspring", {"start": v(2.9, 23.1) * mm, "mid": v(1.7, 23.22) * mm, "end": v(0.49, 23.28) * mm});
            skArc(sketch, "E13.trimOffspring", {"start": v(8.78, 21.56) * mm, "mid": v(7.65, 22) * mm, "end": v(6.5, 22.36) * mm});
            skArc(sketch, "E14.trimOffspring", {"start": v(14.06, 18.56) * mm, "mid": v(13.08, 19.26) * mm, "end": v(12.06, 19.92) * mm});
            skArc(sketch, "E15.trimOffspring", {"start": v(-9.04, 21.46) * mm, "mid": v(-10.14, 20.96) * mm, "end": v(-11.22, 20.4) * mm});
            skArc(sketch, "E16.trimOffspring", {"start": v(18.39, 14.28) * mm, "mid": v(17.62, 15.22) * mm, "end": v(16.8, 16.12) * mm});
            skArc(sketch, "E17.trimOffspring", {"start": v(21.46, 9.04) * mm, "mid": v(20.96, 10.14) * mm, "end": v(20.4, 11.22) * mm});
            skArc(sketch, "E18.trimOffspring", {"start": v(-14.28, 18.39) * mm, "mid": v(-15.22, 17.62) * mm, "end": v(-16.12, 16.8) * mm});
            skArc(sketch, "E19.trimOffspring", {"start": v(-18.56, 14.06) * mm, "mid": v(-19.26, 13.08) * mm, "end": v(-19.92, 12.06) * mm});
            skArc(sketch, "E20.trimOffspring", {"start": v(-21.56, 8.78) * mm, "mid": v(-22, 7.65) * mm, "end": v(-22.36, 6.5) * mm});
            skArc(sketch, "E21.trimOffspring", {"start": v(-23.1, 2.9) * mm, "mid": v(-23.22, 1.7) * mm, "end": v(-23.28, 0.49) * mm});
            skArc(sketch, "E22.trimOffspring", {"start": v(-23.07, -3.18) * mm, "mid": v(-22.87, -4.37) * mm, "end": v(-22.61, -5.55) * mm});
            skArc(sketch, "E23.trimOffspring", {"start": v(-21.46, -9.04) * mm, "mid": v(-20.96, -10.14) * mm, "end": v(-20.4, -11.22) * mm});
            skArc(sketch, "E24.trimOffspring", {"start": v(-18.39, -14.28) * mm, "mid": v(-17.62, -15.22) * mm, "end": v(-16.8, -16.12) * mm});
            skArc(sketch, "E25.trimOffspring", {"start": v(23.07, 3.18) * mm, "mid": v(22.87, 4.37) * mm, "end": v(22.61, 5.55) * mm});
            skArc(sketch, "E26.trimOffspring", {"start": v(23.1, -2.9) * mm, "mid": v(23.22, -1.7) * mm, "end": v(23.28, -0.49) * mm});
            skArc(sketch, "E27.trimOffspring", {"start": v(21.56, -8.78) * mm, "mid": v(22, -7.65) * mm, "end": v(22.36, -6.5) * mm});
            skArc(sketch, "E28.trimOffspring", {"start": v(18.56, -14.06) * mm, "mid": v(19.26, -13.08) * mm, "end": v(19.92, -12.06) * mm});
            skArc(sketch, "E29.trimOffspring", {"start": v(-14.06, -18.56) * mm, "mid": v(-10.45, -20.8) * mm, "end": v(-6.5, -22.36) * mm});
            skArc(sketch, "E30.trimOffspring", {"start": v(14.28, -18.39) * mm, "mid": v(15.22, -17.62) * mm, "end": v(16.12, -16.8) * mm});
            skArc(sketch, "E31.trimOffspring", {"start": v(9.04, -21.46) * mm, "mid": v(10.14, -20.96) * mm, "end": v(11.22, -20.4) * mm});
            skArc(sketch, "E32.trimOffspring", {"start": v(3.18, -23.07) * mm, "mid": v(4.37, -22.87) * mm, "end": v(5.55, -22.61) * mm});
            skArc(sketch, "E33.trimOffspring", {"start": v(-2.9, -23.1) * mm, "mid": v(-1.7, -23.22) * mm, "end": v(-0.49, -23.28) * mm});
            skSolve(sketch);
        }
        {
            var Q0;
            Q0=qSketchRegion(id+"F0",true);
            extrude(context, id + "F1", {"entities" : qUnion([Q0]), "depth" : 12.7 * mm});
        }
        {
            var Q0;
            Q0=makeQuery(id+"F1.opExtrude","CAP_FACE",FACE,{"disambiguationData":[OSD([sQuery(id+"F0.wireOp",EDGE,"E0"),sQuery(id+"F0.wireOp",EDGE,"E1.trimOffspring"),sQuery(id+"F0.wireOp",EDGE,"E2"),sQuery(id+"F0.wireOp",EDGE,"E3"),sQuery(id+"F0.wireOp",EDGE,"E4.MirrorCS"),sQuery(id+"F0.wireOp",EDGE,"E5.MirrorCS"),sQuery(id+"F0.wireOp",EDGE,"E6.MirrorCS"),sQuery(id+"F0.wireOp",EDGE,"E7.filletArc"),sQuery(id+"F0.wireOp",EDGE,"E8.filletArc"),sQuery(id+"F0.wireOp",EDGE,"E9.filletArc"),sQuery(id+"F0.wireOp",EDGE,"E10.filletArc"),sQuery(id+"F0.wireOp",EDGE,"E11.1.2"),sQuery(id+"F0.wireOp",EDGE,"E11.1.3"),sQuery(id+"F0.wireOp",EDGE,"E11.1.4"),sQuery(id+"F0.wireOp",EDGE,"E11.1.6"),sQuery(id+"F0.wireOp",EDGE,"E11.1.7"),sQuery(id+"F0.wireOp",EDGE,"E11.1.8"),sQuery(id+"F0.wireOp",EDGE,"E11.1.9"),sQuery(id+"F0.wireOp",EDGE,"E11.1.10"),sQuery(id+"F0.wireOp",EDGE,"E11.1.11"),sQuery(id+"F0.wireOp",EDGE,"E11.1.12"),sQuery(id+"F0.wireOp",EDGE,"E11.2.2"),sQuery(id+"F0.wireOp",EDGE,"E11.2.3"),sQuery(id+"F0.wireOp",EDGE,"E11.2.4"),sQuery(id+"F0.wireOp",EDGE,"E11.2.6"),sQuery(id+"F0.wireOp",EDGE,"E11.2.7"),sQuery(id+"F0.wireOp",EDGE,"E11.2.8"),sQuery(id+"F0.wireOp",EDGE,"E11.2.9"),sQuery(id+"F0.wireOp",EDGE,"E11.2.10"),sQuery(id+"F0.wireOp",EDGE,"E11.2.11"),sQuery(id+"F0.wireOp",EDGE,"E11.2.12"),sQuery(id+"F0.wireOp",EDGE,"E11.3.2"),sQuery(id+"F0.wireOp",EDGE,"E11.3.3"),sQuery(id+"F0.wireOp",EDGE,"E11.3.4"),sQuery(id+"F0.wireOp",EDGE,"E11.3.6"),sQuery(id+"F0.wireOp",EDGE,"E11.3.7"),sQuery(id+"F0.wireOp",EDGE,"E11.3.8"),sQuery(id+"F0.wireOp",EDGE,"E11.3.9"),sQuery(id+"F0.wireOp",EDGE,"E11.3.10"),sQuery(id+"F0.wireOp",EDGE,"E11.3.11"),sQuery(id+"F0.wireOp",EDGE,"E11.3.12"),sQuery(id+"F0.wireOp",EDGE,"E11.4.2"),sQuery(id+"F0.wireOp",EDGE,"E11.4.3"),sQuery(id+"F0.wireOp",EDGE,"E11.4.4"),sQuery(id+"F0.wireOp",EDGE,"E11.4.6"),sQuery(id+"F0.wireOp",EDGE,"E11.4.7"),sQuery(id+"F0.wireOp",EDGE,"E11.4.8"),sQuery(id+"F0.wireOp",EDGE,"E11.4.9"),sQuery(id+"F0.wireOp",EDGE,"E11.4.10"),sQuery(id+"F0.wireOp",EDGE,"E11.4.11"),sQuery(id+"F0.wireOp",EDGE,"E11.4.12"),sQuery(id+"F0.wireOp",EDGE,"E11.5.2"),sQuery(id+"F0.wireOp",EDGE,"E11.5.3"),sQuery(id+"F0.wireOp",EDGE,"E11.5.4"),sQuery(id+"F0.wireOp",EDGE,"E11.5.6"),sQuery(id+"F0.wireOp",EDGE,"E11.5.7"),sQuery(id+"F0.wireOp",EDGE,"E11.5.8"),sQuery(id+"F0.wireOp",EDGE,"E11.5.9"),sQuery(id+"F0.wireOp",EDGE,"E11.5.10"),sQuery(id+"F0.wireOp",EDGE,"E11.5.11"),sQuery(id+"F0.wireOp",EDGE,"E11.5.12"),sQuery(id+"F0.wireOp",EDGE,"E11.6.2"),sQuery(id+"F0.wireOp",EDGE,"E11.6.3"),sQuery(id+"F0.wireOp",EDGE,"E11.6.4"),sQuery(id+"F0.wireOp",EDGE,"E11.6.6"),sQuery(id+"F0.wireOp",EDGE,"E11.6.7"),sQuery(id+"F0.wireOp",EDGE,"E11.6.8"),sQuery(id+"F0.wireOp",EDGE,"E11.6.9"),sQuery(id+"F0.wireOp",EDGE,"E11.6.10"),sQuery(id+"F0.wireOp",EDGE,"E11.6.11"),sQuery(id+"F0.wireOp",EDGE,"E11.6.12"),sQuery(id+"F0.wireOp",EDGE,"E11.7.2"),sQuery(id+"F0.wireOp",EDGE,"E11.7.3"),sQuery(id+"F0.wireOp",EDGE,"E11.7.4"),sQuery(id+"F0.wireOp",EDGE,"E11.7.6"),sQuery(id+"F0.wireOp",EDGE,"E11.7.7"),sQuery(id+"F0.wireOp",EDGE,"E11.7.8"),sQuery(id+"F0.wireOp",EDGE,"E11.7.9"),sQuery(id+"F0.wireOp",EDGE,"E11.7.10"),sQuery(id+"F0.wireOp",EDGE,"E11.7.11"),sQuery(id+"F0.wireOp",EDGE,"E11.7.12"),sQuery(id+"F0.wireOp",EDGE,"E11.8.2"),sQuery(id+"F0.wireOp",EDGE,"E11.8.3"),sQuery(id+"F0.wireOp",EDGE,"E11.8.4"),sQuery(id+"F0.wireOp",EDGE,"E11.8.6"),sQuery(id+"F0.wireOp",EDGE,"E11.8.7"),sQuery(id+"F0.wireOp",EDGE,"E11.8.8"),sQuery(id+"F0.wireOp",EDGE,"E11.8.9"),sQuery(id+"F0.wireOp",EDGE,"E11.8.10"),sQuery(id+"F0.wireOp",EDGE,"E11.8.11"),sQuery(id+"F0.wireOp",EDGE,"E11.8.12"),sQuery(id+"F0.wireOp",EDGE,"E11.9.2"),sQuery(id+"F0.wireOp",EDGE,"E11.9.3"),sQuery(id+"F0.wireOp",EDGE,"E11.9.4"),sQuery(id+"F0.wireOp",EDGE,"E11.9.6"),sQuery(id+"F0.wireOp",EDGE,"E11.9.7"),sQuery(id+"F0.wireOp",EDGE,"E11.9.8"),sQuery(id+"F0.wireOp",EDGE,"E11.9.9"),sQuery(id+"F0.wireOp",EDGE,"E11.9.10"),sQuery(id+"F0.wireOp",EDGE,"E11.9.11"),sQuery(id+"F0.wireOp",EDGE,"E11.9.12"),sQuery(id+"F0.wireOp",EDGE,"E11.10.2"),sQuery(id+"F0.wireOp",EDGE,"E11.10.3"),sQuery(id+"F0.wireOp",EDGE,"E11.10.4"),sQuery(id+"F0.wireOp",EDGE,"E11.10.6"),sQuery(id+"F0.wireOp",EDGE,"E11.10.7"),sQuery(id+"F0.wireOp",EDGE,"E11.10.8"),sQuery(id+"F0.wireOp",EDGE,"E11.10.9"),sQuery(id+"F0.wireOp",EDGE,"E11.10.10"),sQuery(id+"F0.wireOp",EDGE,"E11.10.11"),sQuery(id+"F0.wireOp",EDGE,"E11.10.12"),sQuery(id+"F0.wireOp",EDGE,"E11.11.2"),sQuery(id+"F0.wireOp",EDGE,"E11.11.3"),sQuery(id+"F0.wireOp",EDGE,"E11.11.4"),sQuery(id+"F0.wireOp",EDGE,"E11.11.6"),sQuery(id+"F0.wireOp",EDGE,"E11.11.7"),sQuery(id+"F0.wireOp",EDGE,"E11.11.8"),sQuery(id+"F0.wireOp",EDGE,"E11.11.9"),sQuery(id+"F0.wireOp",EDGE,"E11.11.10"),sQuery(id+"F0.wireOp",EDGE,"E11.11.11"),sQuery(id+"F0.wireOp",EDGE,"E11.11.12"),sQuery(id+"F0.wireOp",EDGE,"E11.12.2"),sQuery(id+"F0.wireOp",EDGE,"E11.12.3"),sQuery(id+"F0.wireOp",EDGE,"E11.12.4"),sQuery(id+"F0.wireOp",EDGE,"E11.12.6"),sQuery(id+"F0.wireOp",EDGE,"E11.12.7"),sQuery(id+"F0.wireOp",EDGE,"E11.12.8"),sQuery(id+"F0.wireOp",EDGE,"E11.12.9"),sQuery(id+"F0.wireOp",EDGE,"E11.12.10"),sQuery(id+"F0.wireOp",EDGE,"E11.12.11"),sQuery(id+"F0.wireOp",EDGE,"E11.12.12"),sQuery(id+"F0.wireOp",EDGE,"E11.13.2"),sQuery(id+"F0.wireOp",EDGE,"E11.13.3"),sQuery(id+"F0.wireOp",EDGE,"E11.13.4"),sQuery(id+"F0.wireOp",EDGE,"E11.13.6"),sQuery(id+"F0.wireOp",EDGE,"E11.13.7"),sQuery(id+"F0.wireOp",EDGE,"E11.13.8"),sQuery(id+"F0.wireOp",EDGE,"E11.13.9"),sQuery(id+"F0.wireOp",EDGE,"E11.13.10"),sQuery(id+"F0.wireOp",EDGE,"E11.13.11"),sQuery(id+"F0.wireOp",EDGE,"E11.13.12"),sQuery(id+"F0.wireOp",EDGE,"E11.14.2"),sQuery(id+"F0.wireOp",EDGE,"E11.14.3"),sQuery(id+"F0.wireOp",EDGE,"E11.14.4"),sQuery(id+"F0.wireOp",EDGE,"E11.14.6"),sQuery(id+"F0.wireOp",EDGE,"E11.14.7"),sQuery(id+"F0.wireOp",EDGE,"E11.14.8"),sQuery(id+"F0.wireOp",EDGE,"E11.14.9"),sQuery(id+"F0.wireOp",EDGE,"E11.14.10"),sQuery(id+"F0.wireOp",EDGE,"E11.14.11"),sQuery(id+"F0.wireOp",EDGE,"E11.14.12"),sQuery(id+"F0.wireOp",EDGE,"E11.15.2"),sQuery(id+"F0.wireOp",EDGE,"E11.15.3"),sQuery(id+"F0.wireOp",EDGE,"E11.15.4"),sQuery(id+"F0.wireOp",EDGE,"E11.15.6"),sQuery(id+"F0.wireOp",EDGE,"E11.15.7"),sQuery(id+"F0.wireOp",EDGE,"E11.15.8"),sQuery(id+"F0.wireOp",EDGE,"E11.15.9"),sQuery(id+"F0.wireOp",EDGE,"E11.15.10"),sQuery(id+"F0.wireOp",EDGE,"E11.15.11"),sQuery(id+"F0.wireOp",EDGE,"E11.15.12"),sQuery(id+"F0.wireOp",EDGE,"E11.16.2"),sQuery(id+"F0.wireOp",EDGE,"E11.16.3"),sQuery(id+"F0.wireOp",EDGE,"E11.16.4"),sQuery(id+"F0.wireOp",EDGE,"E11.16.6"),sQuery(id+"F0.wireOp",EDGE,"E11.16.7"),sQuery(id+"F0.wireOp",EDGE,"E11.16.8"),sQuery(id+"F0.wireOp",EDGE,"E11.16.9"),sQuery(id+"F0.wireOp",EDGE,"E11.16.10"),sQuery(id+"F0.wireOp",EDGE,"E11.16.11"),sQuery(id+"F0.wireOp",EDGE,"E11.16.12"),sQuery(id+"F0.wireOp",EDGE,"E11.17.2"),sQuery(id+"F0.wireOp",EDGE,"E11.17.3"),sQuery(id+"F0.wireOp",EDGE,"E11.17.4"),sQuery(id+"F0.wireOp",EDGE,"E11.17.6"),sQuery(id+"F0.wireOp",EDGE,"E11.17.7"),sQuery(id+"F0.wireOp",EDGE,"E11.17.8"),sQuery(id+"F0.wireOp",EDGE,"E11.17.9"),sQuery(id+"F0.wireOp",EDGE,"E11.17.10"),sQuery(id+"F0.wireOp",EDGE,"E11.17.11"),sQuery(id+"F0.wireOp",EDGE,"E11.17.12"),sQuery(id+"F0.wireOp",EDGE,"E11.18.2"),sQuery(id+"F0.wireOp",EDGE,"E11.18.3"),sQuery(id+"F0.wireOp",EDGE,"E11.18.4"),sQuery(id+"F0.wireOp",EDGE,"E11.18.6"),sQuery(id+"F0.wireOp",EDGE,"E11.18.7"),sQuery(id+"F0.wireOp",EDGE,"E11.18.8"),sQuery(id+"F0.wireOp",EDGE,"E11.18.9"),sQuery(id+"F0.wireOp",EDGE,"E11.18.10"),sQuery(id+"F0.wireOp",EDGE,"E11.18.11"),sQuery(id+"F0.wireOp",EDGE,"E11.18.12"),sQuery(id+"F0.wireOp",EDGE,"E11.19.2"),sQuery(id+"F0.wireOp",EDGE,"E11.19.3"),sQuery(id+"F0.wireOp",EDGE,"E11.19.4"),sQuery(id+"F0.wireOp",EDGE,"E11.19.6"),sQuery(id+"F0.wireOp",EDGE,"E11.19.7"),sQuery(id+"F0.wireOp",EDGE,"E11.19.8"),sQuery(id+"F0.wireOp",EDGE,"E11.19.9"),sQuery(id+"F0.wireOp",EDGE,"E11.19.10"),sQuery(id+"F0.wireOp",EDGE,"E11.19.11"),sQuery(id+"F0.wireOp",EDGE,"E11.19.12"),sQuery(id+"F0.wireOp",EDGE,"E11.20.2"),sQuery(id+"F0.wireOp",EDGE,"E11.20.3"),sQuery(id+"F0.wireOp",EDGE,"E11.20.4"),sQuery(id+"F0.wireOp",EDGE,"E11.20.6"),sQuery(id+"F0.wireOp",EDGE,"E11.20.7"),sQuery(id+"F0.wireOp",EDGE,"E11.20.8"),sQuery(id+"F0.wireOp",EDGE,"E11.20.9"),sQuery(id+"F0.wireOp",EDGE,"E11.20.10"),sQuery(id+"F0.wireOp",EDGE,"E11.20.11"),sQuery(id+"F0.wireOp",EDGE,"E11.20.12"),sQuery(id+"F0.wireOp",EDGE,"E11.21.2"),sQuery(id+"F0.wireOp",EDGE,"E11.21.3"),sQuery(id+"F0.wireOp",EDGE,"E11.21.4"),sQuery(id+"F0.wireOp",EDGE,"E11.21.6"),sQuery(id+"F0.wireOp",EDGE,"E11.21.7"),sQuery(id+"F0.wireOp",EDGE,"E11.21.8"),sQuery(id+"F0.wireOp",EDGE,"E11.21.9"),sQuery(id+"F0.wireOp",EDGE,"E11.21.10"),sQuery(id+"F0.wireOp",EDGE,"E11.21.11"),sQuery(id+"F0.wireOp",EDGE,"E11.21.12"),sQuery(id+"F0.wireOp",EDGE,"E11.22.2"),sQuery(id+"F0.wireOp",EDGE,"E11.22.3"),sQuery(id+"F0.wireOp",EDGE,"E11.22.4"),sQuery(id+"F0.wireOp",EDGE,"E11.22.6"),sQuery(id+"F0.wireOp",EDGE,"E11.22.7"),sQuery(id+"F0.wireOp",EDGE,"E11.22.8"),sQuery(id+"F0.wireOp",EDGE,"E11.22.9"),sQuery(id+"F0.wireOp",EDGE,"E11.22.10"),sQuery(id+"F0.wireOp",EDGE,"E11.22.11"),sQuery(id+"F0.wireOp",EDGE,"E11.22.12"),sQuery(id+"F0.wireOp",EDGE,"E11.23.2"),sQuery(id+"F0.wireOp",EDGE,"E11.23.3"),sQuery(id+"F0.wireOp",EDGE,"E11.23.4"),sQuery(id+"F0.wireOp",EDGE,"E11.23.6"),sQuery(id+"F0.wireOp",EDGE,"E11.23.7"),sQuery(id+"F0.wireOp",EDGE,"E11.23.8"),sQuery(id+"F0.wireOp",EDGE,"E11.23.9"),sQuery(id+"F0.wireOp",EDGE,"E11.23.10"),sQuery(id+"F0.wireOp",EDGE,"E11.23.11"),sQuery(id+"F0.wireOp",EDGE,"E11.23.12"),sQuery(id+"F0.wireOp",EDGE,"E12.trimOffspring"),sQuery(id+"F0.wireOp",EDGE,"E13.trimOffspring"),sQuery(id+"F0.wireOp",EDGE,"E14.trimOffspring"),sQuery(id+"F0.wireOp",EDGE,"E15.trimOffspring"),sQuery(id+"F0.wireOp",EDGE,"E16.trimOffspring"),sQuery(id+"F0.wireOp",EDGE,"E17.trimOffspring"),sQuery(id+"F0.wireOp",EDGE,"E18.trimOffspring"),sQuery(id+"F0.wireOp",EDGE,"E19.trimOffspring"),sQuery(id+"F0.wireOp",EDGE,"E20.trimOffspring"),sQuery(id+"F0.wireOp",EDGE,"E21.trimOffspring"),sQuery(id+"F0.wireOp",EDGE,"E22.trimOffspring"),sQuery(id+"F0.wireOp",EDGE,"E23.trimOffspring"),sQuery(id+"F0.wireOp",EDGE,"E24.trimOffspring"),sQuery(id+"F0.wireOp",EDGE,"E25.trimOffspring"),sQuery(id+"F0.wireOp",EDGE,"E26.trimOffspring"),sQuery(id+"F0.wireOp",EDGE,"E27.trimOffspring"),sQuery(id+"F0.wireOp",EDGE,"E28.trimOffspring"),sQuery(id+"F0.wireOp",EDGE,"E29.trimOffspring"),sQuery(id+"F0.wireOp",EDGE,"E30.trimOffspring"),sQuery(id+"F0.wireOp",EDGE,"E31.trimOffspring"),sQuery(id+"F0.wireOp",EDGE,"E32.trimOffspring"),sQuery(id+"F0.wireOp",EDGE,"E33.trimOffspring")])],"isStart":false});
            var sketch = newSketch(context, id + "F2", { "sketchPlane" : qUnion([Q0])});
            skCircle(sketch, "E34", {"center": v(0, 0) * mm, "radius": 3.18 * mm});
            skCircle(sketch, "E35", {"center": v(0, 0) * mm, "radius": 3.94 * mm});
            skSolve(sketch);
        }
        {
            var Q0;
            Q0=makeQuery(id+"F2.imprint","IMPRINT",FACE,{"disambiguationData":[TD([[makeQuery(id+"F2.imprint","IMPRINT",EDGE,{"derivedFrom":sQuery(id+"F2.wireOp",EDGE,"E34")}),-1.0]])]});
            extrude(context, id + "F3", {"entities" : qUnion([Q0]), "operationType" : NewBodyOperationType.ADD, "depth" : 12.7 * mm});
        }
        {
            var Q0;
            {var subQ0=sQuery(id+"F0.wireOp",EDGE,"E11.19.6");var subQ1=sQuery(id+"F0.wireOp",EDGE,"E11.3.7");var subQ2=sQuery(id+"F0.wireOp",EDGE,"E11.19.4");var subQ3=sQuery(id+"F0.wireOp",EDGE,"E11.2.8");var subQ4=sQuery(id+"F0.wireOp",EDGE,"E11.23.7");var subQ5=sQuery(id+"F0.wireOp",EDGE,"E11.19.3");var subQ6=sQuery(id+"F0.wireOp",EDGE,"E11.23.6");var subQ7=sQuery(id+"F0.wireOp",EDGE,"E11.19.2");var subQ8=sQuery(id+"F0.wireOp",EDGE,"E11.18.12");var subQ9=sQuery(id+"F0.wireOp",EDGE,"E11.18.10");var subQ10=sQuery(id+"F0.wireOp",EDGE,"E11.18.9");var subQ11=sQuery(id+"F0.wireOp",EDGE,"E11.14.7");var subQ12=sQuery(id+"F0.wireOp",EDGE,"E11.2.10");var subQ13=sQuery(id+"F0.wireOp",EDGE,"E11.18.8");var subQ14=sQuery(id+"F0.wireOp",EDGE,"E11.14.6");var subQ15=sQuery(id+"F0.wireOp",EDGE,"E11.18.7");var subQ16=sQuery(id+"F0.wireOp",EDGE,"E11.1.10");var subQ17=sQuery(id+"F0.wireOp",EDGE,"E11.22.9");var subQ18=sQuery(id+"F0.wireOp",EDGE,"E11.18.6");var subQ19=sQuery(id+"F0.wireOp",EDGE,"E11.17.10");var subQ20=sQuery(id+"F0.wireOp",EDGE,"E11.17.9");var subQ21=sQuery(id+"F0.wireOp",EDGE,"E10.filletArc");var subQ22=sQuery(id+"F0.wireOp",EDGE,"E11.21.11");var subQ23=sQuery(id+"F0.wireOp",EDGE,"E11.17.8");var subQ24=sQuery(id+"F0.wireOp",EDGE,"E11.21.10");var subQ25=sQuery(id+"F0.wireOp",EDGE,"E11.17.7");var subQ26=sQuery(id+"F0.wireOp",EDGE,"E11.5.10");var subQ27=sQuery(id+"F0.wireOp",EDGE,"E11.17.6");var subQ28=sQuery(id+"F0.wireOp",EDGE,"E11.13.3");var subQ29=sQuery(id+"F0.wireOp",EDGE,"E11.17.3");var subQ30=sQuery(id+"F0.wireOp",EDGE,"E11.1.4");var subQ31=sQuery(id+"F0.wireOp",EDGE,"E11.21.6");var subQ32=sQuery(id+"F0.wireOp",EDGE,"E11.16.12");var subQ33=sQuery(id+"F0.wireOp",EDGE,"E11.12.10");var subQ34=sQuery(id+"F0.wireOp",EDGE,"E11.16.11");var subQ35=sQuery(id+"F0.wireOp",EDGE,"E11.9.6");var subQ36=sQuery(id+"F0.wireOp",EDGE,"E11.16.8");var subQ37=sQuery(id+"F0.wireOp",EDGE,"E11.16.4");var subQ38=sQuery(id+"F0.wireOp",EDGE,"E11.16.3");var subQ39=sQuery(id+"F0.wireOp",EDGE,"E11.23.9");var subQ40=sQuery(id+"F0.wireOp",EDGE,"E11.16.2");var subQ41=sQuery(id+"F0.wireOp",EDGE,"E11.20.4");var subQ42=sQuery(id+"F0.wireOp",EDGE,"E11.18.11");var subQ43=sQuery(id+"F0.wireOp",EDGE,"E11.2.3");var subQ44=sQuery(id+"F0.wireOp",EDGE,"E11.23.2");var subQ45=sQuery(id+"F0.wireOp",EDGE,"E11.15.12");var subQ46=sQuery(id+"F0.wireOp",EDGE,"E11.4.4");var subQ47=sQuery(id+"F0.wireOp",EDGE,"E11.20.3");var subQ48=sQuery(id+"F0.wireOp",EDGE,"E11.17.4");var subQ49=sQuery(id+"F0.wireOp",EDGE,"E11.9.10");var subQ50=sQuery(id+"F0.wireOp",EDGE,"E11.15.10");var subQ51=sQuery(id+"F0.wireOp",EDGE,"E11.23.4");var subQ52=sQuery(id+"F0.wireOp",EDGE,"E11.15.9");var subQ53=sQuery(id+"F0.wireOp",EDGE,"E11.19.11");var subQ54=sQuery(id+"F0.wireOp",EDGE,"E11.15.2");var subQ55=sQuery(id+"F0.wireOp",EDGE,"E11.14.10");var subQ56=sQuery(id+"F0.wireOp",EDGE,"E11.14.9");var subQ57=sQuery(id+"F0.wireOp",EDGE,"E11.14.8");var subQ58=sQuery(id+"F0.wireOp",EDGE,"E11.19.7");var subQ59=sQuery(id+"F0.wireOp",EDGE,"E11.15.4");var subQ60=sQuery(id+"F0.wireOp",EDGE,"E11.14.4");var subQ61=sQuery(id+"F0.wireOp",EDGE,"E11.17.2");var subQ62=sQuery(id+"F0.wireOp",EDGE,"E11.12.11");var subQ63=sQuery(id+"F0.wireOp",EDGE,"E11.14.3");var subQ64=sQuery(id+"F0.wireOp",EDGE,"E11.9.12");var subQ65=sQuery(id+"F0.wireOp",EDGE,"E11.13.11");var subQ66=sQuery(id+"F0.wireOp",EDGE,"E11.9.9");var subQ67=sQuery(id+"F0.wireOp",EDGE,"E11.15.6");var subQ68=sQuery(id+"F0.wireOp",EDGE,"E11.11.3");var subQ69=sQuery(id+"F0.wireOp",EDGE,"E11.13.4");var subQ70=sQuery(id+"F0.wireOp",EDGE,"E11.18.3");var subQ71=sQuery(id+"F0.wireOp",EDGE,"E11.13.12");var subQ72=sQuery(id+"F0.wireOp",EDGE,"E11.13.2");var subQ73=sQuery(id+"F0.wireOp",EDGE,"E11.15.11");var subQ74=sQuery(id+"F0.wireOp",EDGE,"E11.11.9");var subQ75=sQuery(id+"F0.wireOp",EDGE,"E11.12.12");var subQ76=sQuery(id+"F0.wireOp",EDGE,"E11.15.8");var subQ77=sQuery(id+"F0.wireOp",EDGE,"E11.12.9");var subQ78=sQuery(id+"F0.wireOp",EDGE,"E11.8.7");var subQ79=sQuery(id+"F0.wireOp",EDGE,"E11.15.7");var subQ80=sQuery(id+"F0.wireOp",EDGE,"E11.11.4");var subQ81=sQuery(id+"F0.wireOp",EDGE,"E11.12.8");var subQ82=sQuery(id+"F0.wireOp",EDGE,"E11.12.6");var subQ83=sQuery(id+"F0.wireOp",EDGE,"E11.18.4");var subQ84=sQuery(id+"F0.wireOp",EDGE,"E11.2.6");var subQ85=sQuery(id+"F0.wireOp",EDGE,"E11.11.10");var subQ86=sQuery(id+"F0.wireOp",EDGE,"E11.16.9");var subQ87=sQuery(id+"F0.wireOp",EDGE,"E11.12.7");var subQ88=sQuery(id+"F0.wireOp",EDGE,"E11.13.10");var subQ89=sQuery(id+"F0.wireOp",EDGE,"E11.9.8");var subQ90=sQuery(id+"F0.wireOp",EDGE,"E11.11.8");var subQ91=sQuery(id+"F0.wireOp",EDGE,"E11.11.7");var subQ92=sQuery(id+"F0.wireOp",EDGE,"E11.17.11");var subQ93=sQuery(id+"F0.wireOp",EDGE,"E11.1.12");var subQ94=sQuery(id+"F0.wireOp",EDGE,"E11.11.6");var subQ95=sQuery(id+"F0.wireOp",EDGE,"E11.7.3");var subQ96=sQuery(id+"F0.wireOp",EDGE,"E11.13.6");var subQ97=sQuery(id+"F0.wireOp",EDGE,"E11.14.2");var subQ98=sQuery(id+"F0.wireOp",EDGE,"E11.11.2");var subQ99=sQuery(id+"F0.wireOp",EDGE,"E11.10.12");var subQ100=sQuery(id+"F0.wireOp",EDGE,"E11.6.10");var subQ101=sQuery(id+"F0.wireOp",EDGE,"E11.10.8");var subQ102=sQuery(id+"F0.wireOp",EDGE,"E11.6.6");var subQ103=sQuery(id+"F0.wireOp",EDGE,"E11.19.9");var subQ104=sQuery(id+"F0.wireOp",EDGE,"E11.16.10");var subQ105=sQuery(id+"F0.wireOp",EDGE,"E9.filletArc");var subQ106=sQuery(id+"F0.wireOp",EDGE,"E11.20.12");var subQ107=sQuery(id+"F0.wireOp",EDGE,"E11.10.4");var subQ108=sQuery(id+"F0.wireOp",EDGE,"E32.trimOffspring");var subQ109=sQuery(id+"F0.wireOp",EDGE,"E11.19.8");var subQ110=sQuery(id+"F0.wireOp",EDGE,"E11.10.3");var subQ111=sQuery(id+"F0.wireOp",EDGE,"E11.10.2");var subQ112=sQuery(id+"F0.wireOp",EDGE,"E11.14.12");var subQ113=sQuery(id+"F0.wireOp",EDGE,"E11.10.10");var subQ114=sQuery(id+"F0.wireOp",EDGE,"E11.13.9");var subQ115=sQuery(id+"F0.wireOp",EDGE,"E11.4.2");var subQ116=sQuery(id+"F0.wireOp",EDGE,"E11.4.8");var subQ117=sQuery(id+"F0.wireOp",EDGE,"E4.MirrorCS");var subQ118=sQuery(id+"F0.wireOp",EDGE,"E11.3.10");var subQ119=sQuery(id+"F0.wireOp",EDGE,"E11.13.7");var subQ120=sQuery(id+"F0.wireOp",EDGE,"E11.9.4");var subQ121=sQuery(id+"F0.wireOp",EDGE,"E11.4.6");var subQ122=sQuery(id+"F0.wireOp",EDGE,"E11.3.6");var subQ123=sQuery(id+"F0.wireOp",EDGE,"E11.10.11");var subQ124=sQuery(id+"F0.wireOp",EDGE,"E11.8.2");var subQ125=sQuery(id+"F0.wireOp",EDGE,"E11.12.4");var subQ126=sQuery(id+"F0.wireOp",EDGE,"E11.2.12");var subQ127=sQuery(id+"F0.wireOp",EDGE,"E11.10.7");var subQ128=sQuery(id+"F0.wireOp",EDGE,"E11.4.7");var subQ129=sQuery(id+"F0.wireOp",EDGE,"E11.3.9");var subQ130=sQuery(id+"F0.wireOp",EDGE,"E11.12.2");var subQ131=sQuery(id+"F0.wireOp",EDGE,"E11.2.9");var subQ132=sQuery(id+"F0.wireOp",EDGE,"E11.7.11");var subQ133=sQuery(id+"F0.wireOp",EDGE,"E11.11.12");var subQ134=sQuery(id+"F0.wireOp",EDGE,"E11.8.11");var subQ135=sQuery(id+"F0.wireOp",EDGE,"E11.3.4");var subQ136=sQuery(id+"F0.wireOp",EDGE,"E11.7.7");var subQ137=sQuery(id+"F0.wireOp",EDGE,"E11.2.4");var subQ138=sQuery(id+"F0.wireOp",EDGE,"E11.3.3");var subQ139=sQuery(id+"F0.wireOp",EDGE,"E11.7.6");var subQ140=sQuery(id+"F0.wireOp",EDGE,"E12.trimOffspring");var subQ141=sQuery(id+"F0.wireOp",EDGE,"E11.6.2");var subQ142=sQuery(id+"F0.wireOp",EDGE,"E7.filletArc");var subQ143=sQuery(id+"F0.wireOp",EDGE,"E11.21.8");var subQ144=sQuery(id+"F0.wireOp",EDGE,"E11.5.11");var subQ145=sQuery(id+"F0.wireOp",EDGE,"E11.1.9");var subQ146=sQuery(id+"F0.wireOp",EDGE,"E11.1.6");var subQ147=sQuery(id+"F0.wireOp",EDGE,"E11.18.2");var subQ148=sQuery(id+"F0.wireOp",EDGE,"E11.8.9");var subQ149=sQuery(id+"F0.wireOp",EDGE,"E6.MirrorCS");var subQ150=sQuery(id+"F0.wireOp",EDGE,"E11.21.7");var subQ151=sQuery(id+"F0.wireOp",EDGE,"E5.MirrorCS");var subQ152=sQuery(id+"F0.wireOp",EDGE,"E11.16.6");var subQ153=sQuery(id+"F0.wireOp",EDGE,"E11.9.11");var subQ154=sQuery(id+"F0.wireOp",EDGE,"E11.5.9");var subQ155=sQuery(id+"F0.wireOp",EDGE,"E29.trimOffspring");var subQ156=sQuery(id+"F0.wireOp",EDGE,"E11.6.12");var subQ157=sQuery(id+"F0.wireOp",EDGE,"E0");var subQ158=sQuery(id+"F0.wireOp",EDGE,"E11.1.8");var subQ159=sQuery(id+"F0.wireOp",EDGE,"E8.filletArc");var subQ160=sQuery(id+"F0.wireOp",EDGE,"E11.4.12");var subQ161=sQuery(id+"F0.wireOp",EDGE,"E1.trimOffspring");var subQ162=sQuery(id+"F0.wireOp",EDGE,"E11.9.7");var subQ163=sQuery(id+"F0.wireOp",EDGE,"E11.5.4");var subQ164=sQuery(id+"F0.wireOp",EDGE,"E25.trimOffspring");var subQ165=sQuery(id+"F0.wireOp",EDGE,"E11.6.8");var subQ166=sQuery(id+"F0.wireOp",EDGE,"E11.3.2");var subQ167=sQuery(id+"F0.wireOp",EDGE,"E2");var subQ168=sQuery(id+"F0.wireOp",EDGE,"E11.21.2");var subQ169=sQuery(id+"F0.wireOp",EDGE,"E11.13.8");var subQ170=sQuery(id+"F0.wireOp",EDGE,"E11.4.3");var subQ171=sQuery(id+"F0.wireOp",EDGE,"E3");var subQ172=sQuery(id+"F0.wireOp",EDGE,"E11.21.3");var subQ173=sQuery(id+"F0.wireOp",EDGE,"E11.1.2");var subQ174=sQuery(id+"F0.wireOp",EDGE,"E11.21.12");var subQ175=sQuery(id+"F0.wireOp",EDGE,"E11.1.7");var subQ176=sQuery(id+"F0.wireOp",EDGE,"E11.15.3");var subQ177=sQuery(id+"F0.wireOp",EDGE,"E11.10.6");var subQ178=sQuery(id+"F0.wireOp",EDGE,"E11.3.11");var subQ179=sQuery(id+"F0.wireOp",EDGE,"E11.19.10");var subQ180=sQuery(id+"F0.wireOp",EDGE,"E11.9.2");var subQ181=sQuery(id+"F0.wireOp",EDGE,"E11.4.11");var subQ182=sQuery(id+"F0.wireOp",EDGE,"E11.6.3");var subQ183=sQuery(id+"F0.wireOp",EDGE,"E11.6.4");var subQ184=sQuery(id+"F0.wireOp",EDGE,"E11.2.2");var subQ185=sQuery(id+"F0.wireOp",EDGE,"E11.9.3");var subQ186=sQuery(id+"F0.wireOp",EDGE,"E11.20.11");var subQ187=sQuery(id+"F0.wireOp",EDGE,"E11.2.11");var subQ188=sQuery(id+"F0.wireOp",EDGE,"E11.1.11");var subQ189=sQuery(id+"F0.wireOp",EDGE,"E11.3.8");var subQ190=sQuery(id+"F0.wireOp",EDGE,"E11.7.10");var subQ191=sQuery(id+"F0.wireOp",EDGE,"E16.trimOffspring");var subQ192=sQuery(id+"F0.wireOp",EDGE,"E11.6.7");var subQ193=sQuery(id+"F0.wireOp",EDGE,"E11.10.9");var subQ194=sQuery(id+"F0.wireOp",EDGE,"E11.22.6");var subQ195=sQuery(id+"F0.wireOp",EDGE,"E11.1.3");var subQ196=sQuery(id+"F0.wireOp",EDGE,"E11.5.6");var subQ197=sQuery(id+"F0.wireOp",EDGE,"E11.7.8");var subQ198=sQuery(id+"F0.wireOp",EDGE,"E11.4.9");var subQ199=sQuery(id+"F0.wireOp",EDGE,"E27.trimOffspring");var subQ200=sQuery(id+"F0.wireOp",EDGE,"E11.7.9");var subQ201=sQuery(id+"F0.wireOp",EDGE,"E11.4.10");var subQ202=sQuery(id+"F0.wireOp",EDGE,"E11.8.12");var subQ203=sQuery(id+"F0.wireOp",EDGE,"E28.trimOffspring");var subQ204=sQuery(id+"F0.wireOp",EDGE,"E11.7.12");var subQ205=sQuery(id+"F0.wireOp",EDGE,"E11.12.3");var subQ206=sQuery(id+"F0.wireOp",EDGE,"E11.23.11");var subQ207=sQuery(id+"F0.wireOp",EDGE,"E11.5.2");var subQ208=sQuery(id+"F0.wireOp",EDGE,"E30.trimOffspring");var subQ209=sQuery(id+"F0.wireOp",EDGE,"E11.5.3");var subQ210=sQuery(id+"F0.wireOp",EDGE,"E31.trimOffspring");var subQ211=sQuery(id+"F0.wireOp",EDGE,"E11.2.7");var subQ212=sQuery(id+"F0.wireOp",EDGE,"E11.6.9");var subQ213=sQuery(id+"F0.wireOp",EDGE,"E11.11.11");var subQ214=sQuery(id+"F0.wireOp",EDGE,"E11.5.8");var subQ215=sQuery(id+"F0.wireOp",EDGE,"E11.5.12");var subQ216=sQuery(id+"F0.wireOp",EDGE,"E11.3.12");var subQ217=sQuery(id+"F0.wireOp",EDGE,"E11.8.3");var subQ218=sQuery(id+"F0.wireOp",EDGE,"E20.trimOffspring");var subQ219=sQuery(id+"F0.wireOp",EDGE,"E11.6.11");var subQ220=sQuery(id+"F0.wireOp",EDGE,"E11.22.10");var subQ221=sQuery(id+"F0.wireOp",EDGE,"E11.16.7");var subQ222=sQuery(id+"F0.wireOp",EDGE,"E11.7.2");var subQ223=sQuery(id+"F0.wireOp",EDGE,"E11.7.4");var subQ224=sQuery(id+"F0.wireOp",EDGE,"E11.23.3");var subQ225=sQuery(id+"F0.wireOp",EDGE,"E11.8.4");var subQ226=sQuery(id+"F0.wireOp",EDGE,"E11.14.11");var subQ227=sQuery(id+"F0.wireOp",EDGE,"E11.5.7");var subQ228=sQuery(id+"F0.wireOp",EDGE,"E11.8.6");var subQ229=sQuery(id+"F0.wireOp",EDGE,"E14.trimOffspring");var subQ230=sQuery(id+"F0.wireOp",EDGE,"E11.17.12");var subQ231=sQuery(id+"F0.wireOp",EDGE,"E11.8.8");var subQ232=sQuery(id+"F0.wireOp",EDGE,"E24.trimOffspring");var subQ233=sQuery(id+"F0.wireOp",EDGE,"E11.8.10");var subQ234=sQuery(id+"F0.wireOp",EDGE,"E18.trimOffspring");var subQ235=sQuery(id+"F0.wireOp",EDGE,"E11.19.12");var subQ236=sQuery(id+"F0.wireOp",EDGE,"E13.trimOffspring");var subQ237=sQuery(id+"F0.wireOp",EDGE,"E11.20.2");var subQ238=sQuery(id+"F0.wireOp",EDGE,"E11.20.6");var subQ239=sQuery(id+"F0.wireOp",EDGE,"E17.trimOffspring");var subQ240=sQuery(id+"F0.wireOp",EDGE,"E11.20.7");var subQ241=sQuery(id+"F0.wireOp",EDGE,"E11.20.8");var subQ242=sQuery(id+"F0.wireOp",EDGE,"E11.20.9");var subQ243=sQuery(id+"F0.wireOp",EDGE,"E11.20.10");var subQ244=sQuery(id+"F0.wireOp",EDGE,"E21.trimOffspring");var subQ245=sQuery(id+"F0.wireOp",EDGE,"E11.21.4");var subQ246=sQuery(id+"F0.wireOp",EDGE,"E26.trimOffspring");var subQ247=sQuery(id+"F0.wireOp",EDGE,"E11.21.9");var subQ248=sQuery(id+"F0.wireOp",EDGE,"E11.22.2");var subQ249=sQuery(id+"F0.wireOp",EDGE,"E33.trimOffspring");var subQ250=sQuery(id+"F0.wireOp",EDGE,"E11.22.3");var subQ251=sQuery(id+"F0.wireOp",EDGE,"E11.22.4");var subQ252=sQuery(id+"F0.wireOp",EDGE,"E11.22.7");var subQ253=sQuery(id+"F0.wireOp",EDGE,"E11.22.8");var subQ254=sQuery(id+"F0.wireOp",EDGE,"E11.22.11");var subQ255=sQuery(id+"F0.wireOp",EDGE,"E11.22.12");var subQ256=sQuery(id+"F0.wireOp",EDGE,"E11.23.8");var subQ257=sQuery(id+"F0.wireOp",EDGE,"E11.23.10");var subQ258=sQuery(id+"F0.wireOp",EDGE,"E11.23.12");var subQ259=sQuery(id+"F0.wireOp",EDGE,"E15.trimOffspring");var subQ260=sQuery(id+"F0.wireOp",EDGE,"E19.trimOffspring");var subQ261=sQuery(id+"F0.wireOp",EDGE,"E22.trimOffspring");var subQ262=sQuery(id+"F0.wireOp",EDGE,"E23.trimOffspring");Q0=makeQuery(id+"F3.boolean.opBoolean","SPLIT",FACE,{"disambiguationData":[TD([makeQuery(id+"F1.opExtrude","SWEPT_FACE",FACE,{"disambiguationData":[OSD([subQ157])]})])],"derivedFrom":makeQuery(id+"F1.opExtrude","CAP_FACE",FACE,{"disambiguationData":[OSD([subQ157,subQ161,subQ167,subQ171,subQ117,subQ151,subQ149,subQ142,subQ159,subQ105,subQ21,subQ173,subQ195,subQ30,subQ146,subQ175,subQ158,subQ145,subQ16,subQ188,subQ93,subQ184,subQ43,subQ137,subQ84,subQ211,subQ3,subQ131,subQ12,subQ187,subQ126,subQ166,subQ138,subQ135,subQ122,subQ1,subQ189,subQ129,subQ118,subQ178,subQ216,subQ115,subQ170,subQ46,subQ121,subQ128,subQ116,subQ198,subQ201,subQ181,subQ160,subQ207,subQ209,subQ163,subQ196,subQ227,subQ214,subQ154,subQ26,subQ144,subQ215,subQ141,subQ182,subQ183,subQ102,subQ192,subQ165,subQ212,subQ100,subQ219,subQ156,subQ222,subQ95,subQ223,subQ139,subQ136,subQ197,subQ200,subQ190,subQ132,subQ204,subQ124,subQ217,subQ225,subQ228,subQ78,subQ231,subQ148,subQ233,subQ134,subQ202,subQ180,subQ185,subQ120,subQ35,subQ162,subQ89,subQ66,subQ49,subQ153,subQ64,subQ111,subQ110,subQ107,subQ177,subQ127,subQ101,subQ193,subQ113,subQ123,subQ99,subQ98,subQ68,subQ80,subQ94,subQ91,subQ90,subQ74,subQ85,subQ213,subQ133,subQ130,subQ205,subQ125,subQ82,subQ87,subQ81,subQ77,subQ33,subQ62,subQ75,subQ72,subQ28,subQ69,subQ96,subQ119,subQ169,subQ114,subQ88,subQ65,subQ71,subQ97,subQ63,subQ60,subQ14,subQ11,subQ57,subQ56,subQ55,subQ226,subQ112,subQ54,subQ176,subQ59,subQ67,subQ79,subQ76,subQ52,subQ50,subQ73,subQ45,subQ40,subQ38,subQ37,subQ152,subQ221,subQ36,subQ86,subQ104,subQ34,subQ32,subQ61,subQ29,subQ48,subQ27,subQ25,subQ23,subQ20,subQ19,subQ92,subQ230,subQ147,subQ70,subQ83,subQ18,subQ15,subQ13,subQ10,subQ9,subQ42,subQ8,subQ7,subQ5,subQ2,subQ0,subQ58,subQ109,subQ103,subQ179,subQ53,subQ235,subQ237,subQ47,subQ41,subQ238,subQ240,subQ241,subQ242,subQ243,subQ186,subQ106,subQ168,subQ172,subQ245,subQ31,subQ150,subQ143,subQ247,subQ24,subQ22,subQ174,subQ248,subQ250,subQ251,subQ194,subQ252,subQ253,subQ17,subQ220,subQ254,subQ255,subQ44,subQ224,subQ51,subQ6,subQ4,subQ256,subQ39,subQ257,subQ206,subQ258,subQ140,subQ236,subQ229,subQ259,subQ191,subQ239,subQ234,subQ260,subQ218,subQ244,subQ261,subQ262,subQ232,subQ164,subQ246,subQ199,subQ203,subQ155,subQ208,subQ210,subQ108,subQ249])],"isStart":false})});}
            var sketch = newSketch(context, id + "F4", { "sketchPlane" : qUnion([Q0])});
            skPoint(sketch, "E36", {"position": v(0, 0) * mm});
            skSolve(sketch);
        }
        {
            var Q0;
            Q0=sQuery(id+"F4.wireOp",VERTEX,"E36");
            var Q1;
            Q1=makeQuery(id+"F1.opExtrude","SWEPT_BODY",BODY,{"disambiguationData":[OSD([sQuery(id+"F0.wireOp",EDGE,"E0"),sQuery(id+"F0.wireOp",EDGE,"E1.trimOffspring"),sQuery(id+"F0.wireOp",EDGE,"E2"),sQuery(id+"F0.wireOp",EDGE,"E3"),sQuery(id+"F0.wireOp",EDGE,"E4.MirrorCS"),sQuery(id+"F0.wireOp",EDGE,"E5.MirrorCS"),sQuery(id+"F0.wireOp",EDGE,"E6.MirrorCS"),sQuery(id+"F0.wireOp",EDGE,"E7.filletArc"),sQuery(id+"F0.wireOp",EDGE,"E8.filletArc"),sQuery(id+"F0.wireOp",EDGE,"E9.filletArc"),sQuery(id+"F0.wireOp",EDGE,"E10.filletArc"),sQuery(id+"F0.wireOp",EDGE,"E11.1.2"),sQuery(id+"F0.wireOp",EDGE,"E11.1.3"),sQuery(id+"F0.wireOp",EDGE,"E11.1.4"),sQuery(id+"F0.wireOp",EDGE,"E11.1.6"),sQuery(id+"F0.wireOp",EDGE,"E11.1.7"),sQuery(id+"F0.wireOp",EDGE,"E11.1.8"),sQuery(id+"F0.wireOp",EDGE,"E11.1.9"),sQuery(id+"F0.wireOp",EDGE,"E11.1.10"),sQuery(id+"F0.wireOp",EDGE,"E11.1.11"),sQuery(id+"F0.wireOp",EDGE,"E11.1.12"),sQuery(id+"F0.wireOp",EDGE,"E11.2.2"),sQuery(id+"F0.wireOp",EDGE,"E11.2.3"),sQuery(id+"F0.wireOp",EDGE,"E11.2.4"),sQuery(id+"F0.wireOp",EDGE,"E11.2.6"),sQuery(id+"F0.wireOp",EDGE,"E11.2.7"),sQuery(id+"F0.wireOp",EDGE,"E11.2.8"),sQuery(id+"F0.wireOp",EDGE,"E11.2.9"),sQuery(id+"F0.wireOp",EDGE,"E11.2.10"),sQuery(id+"F0.wireOp",EDGE,"E11.2.11"),sQuery(id+"F0.wireOp",EDGE,"E11.2.12"),sQuery(id+"F0.wireOp",EDGE,"E11.3.2"),sQuery(id+"F0.wireOp",EDGE,"E11.3.3"),sQuery(id+"F0.wireOp",EDGE,"E11.3.4"),sQuery(id+"F0.wireOp",EDGE,"E11.3.6"),sQuery(id+"F0.wireOp",EDGE,"E11.3.7"),sQuery(id+"F0.wireOp",EDGE,"E11.3.8"),sQuery(id+"F0.wireOp",EDGE,"E11.3.9"),sQuery(id+"F0.wireOp",EDGE,"E11.3.10"),sQuery(id+"F0.wireOp",EDGE,"E11.3.11"),sQuery(id+"F0.wireOp",EDGE,"E11.3.12"),sQuery(id+"F0.wireOp",EDGE,"E11.4.2"),sQuery(id+"F0.wireOp",EDGE,"E11.4.3"),sQuery(id+"F0.wireOp",EDGE,"E11.4.4"),sQuery(id+"F0.wireOp",EDGE,"E11.4.6"),sQuery(id+"F0.wireOp",EDGE,"E11.4.7"),sQuery(id+"F0.wireOp",EDGE,"E11.4.8"),sQuery(id+"F0.wireOp",EDGE,"E11.4.9"),sQuery(id+"F0.wireOp",EDGE,"E11.4.10"),sQuery(id+"F0.wireOp",EDGE,"E11.4.11"),sQuery(id+"F0.wireOp",EDGE,"E11.4.12"),sQuery(id+"F0.wireOp",EDGE,"E11.5.2"),sQuery(id+"F0.wireOp",EDGE,"E11.5.3"),sQuery(id+"F0.wireOp",EDGE,"E11.5.4"),sQuery(id+"F0.wireOp",EDGE,"E11.5.6"),sQuery(id+"F0.wireOp",EDGE,"E11.5.7"),sQuery(id+"F0.wireOp",EDGE,"E11.5.8"),sQuery(id+"F0.wireOp",EDGE,"E11.5.9"),sQuery(id+"F0.wireOp",EDGE,"E11.5.10"),sQuery(id+"F0.wireOp",EDGE,"E11.5.11"),sQuery(id+"F0.wireOp",EDGE,"E11.5.12"),sQuery(id+"F0.wireOp",EDGE,"E11.6.2"),sQuery(id+"F0.wireOp",EDGE,"E11.6.3"),sQuery(id+"F0.wireOp",EDGE,"E11.6.4"),sQuery(id+"F0.wireOp",EDGE,"E11.6.6"),sQuery(id+"F0.wireOp",EDGE,"E11.6.7"),sQuery(id+"F0.wireOp",EDGE,"E11.6.8"),sQuery(id+"F0.wireOp",EDGE,"E11.6.9"),sQuery(id+"F0.wireOp",EDGE,"E11.6.10"),sQuery(id+"F0.wireOp",EDGE,"E11.6.11"),sQuery(id+"F0.wireOp",EDGE,"E11.6.12"),sQuery(id+"F0.wireOp",EDGE,"E11.7.2"),sQuery(id+"F0.wireOp",EDGE,"E11.7.3"),sQuery(id+"F0.wireOp",EDGE,"E11.7.4"),sQuery(id+"F0.wireOp",EDGE,"E11.7.6"),sQuery(id+"F0.wireOp",EDGE,"E11.7.7"),sQuery(id+"F0.wireOp",EDGE,"E11.7.8"),sQuery(id+"F0.wireOp",EDGE,"E11.7.9"),sQuery(id+"F0.wireOp",EDGE,"E11.7.10"),sQuery(id+"F0.wireOp",EDGE,"E11.7.11"),sQuery(id+"F0.wireOp",EDGE,"E11.7.12"),sQuery(id+"F0.wireOp",EDGE,"E11.8.2"),sQuery(id+"F0.wireOp",EDGE,"E11.8.3"),sQuery(id+"F0.wireOp",EDGE,"E11.8.4"),sQuery(id+"F0.wireOp",EDGE,"E11.8.6"),sQuery(id+"F0.wireOp",EDGE,"E11.8.7"),sQuery(id+"F0.wireOp",EDGE,"E11.8.8"),sQuery(id+"F0.wireOp",EDGE,"E11.8.9"),sQuery(id+"F0.wireOp",EDGE,"E11.8.10"),sQuery(id+"F0.wireOp",EDGE,"E11.8.11"),sQuery(id+"F0.wireOp",EDGE,"E11.8.12"),sQuery(id+"F0.wireOp",EDGE,"E11.9.2"),sQuery(id+"F0.wireOp",EDGE,"E11.9.3"),sQuery(id+"F0.wireOp",EDGE,"E11.9.4"),sQuery(id+"F0.wireOp",EDGE,"E11.9.6"),sQuery(id+"F0.wireOp",EDGE,"E11.9.7"),sQuery(id+"F0.wireOp",EDGE,"E11.9.8"),sQuery(id+"F0.wireOp",EDGE,"E11.9.9"),sQuery(id+"F0.wireOp",EDGE,"E11.9.10"),sQuery(id+"F0.wireOp",EDGE,"E11.9.11"),sQuery(id+"F0.wireOp",EDGE,"E11.9.12"),sQuery(id+"F0.wireOp",EDGE,"E11.10.2"),sQuery(id+"F0.wireOp",EDGE,"E11.10.3"),sQuery(id+"F0.wireOp",EDGE,"E11.10.4"),sQuery(id+"F0.wireOp",EDGE,"E11.10.6"),sQuery(id+"F0.wireOp",EDGE,"E11.10.7"),sQuery(id+"F0.wireOp",EDGE,"E11.10.8"),sQuery(id+"F0.wireOp",EDGE,"E11.10.9"),sQuery(id+"F0.wireOp",EDGE,"E11.10.10"),sQuery(id+"F0.wireOp",EDGE,"E11.10.11"),sQuery(id+"F0.wireOp",EDGE,"E11.10.12"),sQuery(id+"F0.wireOp",EDGE,"E11.11.2"),sQuery(id+"F0.wireOp",EDGE,"E11.11.3"),sQuery(id+"F0.wireOp",EDGE,"E11.11.4"),sQuery(id+"F0.wireOp",EDGE,"E11.11.6"),sQuery(id+"F0.wireOp",EDGE,"E11.11.7"),sQuery(id+"F0.wireOp",EDGE,"E11.11.8"),sQuery(id+"F0.wireOp",EDGE,"E11.11.9"),sQuery(id+"F0.wireOp",EDGE,"E11.11.10"),sQuery(id+"F0.wireOp",EDGE,"E11.11.11"),sQuery(id+"F0.wireOp",EDGE,"E11.11.12"),sQuery(id+"F0.wireOp",EDGE,"E11.12.2"),sQuery(id+"F0.wireOp",EDGE,"E11.12.3"),sQuery(id+"F0.wireOp",EDGE,"E11.12.4"),sQuery(id+"F0.wireOp",EDGE,"E11.12.6"),sQuery(id+"F0.wireOp",EDGE,"E11.12.7"),sQuery(id+"F0.wireOp",EDGE,"E11.12.8"),sQuery(id+"F0.wireOp",EDGE,"E11.12.9"),sQuery(id+"F0.wireOp",EDGE,"E11.12.10"),sQuery(id+"F0.wireOp",EDGE,"E11.12.11"),sQuery(id+"F0.wireOp",EDGE,"E11.12.12"),sQuery(id+"F0.wireOp",EDGE,"E11.13.2"),sQuery(id+"F0.wireOp",EDGE,"E11.13.3"),sQuery(id+"F0.wireOp",EDGE,"E11.13.4"),sQuery(id+"F0.wireOp",EDGE,"E11.13.6"),sQuery(id+"F0.wireOp",EDGE,"E11.13.7"),sQuery(id+"F0.wireOp",EDGE,"E11.13.8"),sQuery(id+"F0.wireOp",EDGE,"E11.13.9"),sQuery(id+"F0.wireOp",EDGE,"E11.13.10"),sQuery(id+"F0.wireOp",EDGE,"E11.13.11"),sQuery(id+"F0.wireOp",EDGE,"E11.13.12"),sQuery(id+"F0.wireOp",EDGE,"E11.14.2"),sQuery(id+"F0.wireOp",EDGE,"E11.14.3"),sQuery(id+"F0.wireOp",EDGE,"E11.14.4"),sQuery(id+"F0.wireOp",EDGE,"E11.14.6"),sQuery(id+"F0.wireOp",EDGE,"E11.14.7"),sQuery(id+"F0.wireOp",EDGE,"E11.14.8"),sQuery(id+"F0.wireOp",EDGE,"E11.14.9"),sQuery(id+"F0.wireOp",EDGE,"E11.14.10"),sQuery(id+"F0.wireOp",EDGE,"E11.14.11"),sQuery(id+"F0.wireOp",EDGE,"E11.14.12"),sQuery(id+"F0.wireOp",EDGE,"E11.15.2"),sQuery(id+"F0.wireOp",EDGE,"E11.15.3"),sQuery(id+"F0.wireOp",EDGE,"E11.15.4"),sQuery(id+"F0.wireOp",EDGE,"E11.15.6"),sQuery(id+"F0.wireOp",EDGE,"E11.15.7"),sQuery(id+"F0.wireOp",EDGE,"E11.15.8"),sQuery(id+"F0.wireOp",EDGE,"E11.15.9"),sQuery(id+"F0.wireOp",EDGE,"E11.15.10"),sQuery(id+"F0.wireOp",EDGE,"E11.15.11"),sQuery(id+"F0.wireOp",EDGE,"E11.15.12"),sQuery(id+"F0.wireOp",EDGE,"E11.16.2"),sQuery(id+"F0.wireOp",EDGE,"E11.16.3"),sQuery(id+"F0.wireOp",EDGE,"E11.16.4"),sQuery(id+"F0.wireOp",EDGE,"E11.16.6"),sQuery(id+"F0.wireOp",EDGE,"E11.16.7"),sQuery(id+"F0.wireOp",EDGE,"E11.16.8"),sQuery(id+"F0.wireOp",EDGE,"E11.16.9"),sQuery(id+"F0.wireOp",EDGE,"E11.16.10"),sQuery(id+"F0.wireOp",EDGE,"E11.16.11"),sQuery(id+"F0.wireOp",EDGE,"E11.16.12"),sQuery(id+"F0.wireOp",EDGE,"E11.17.2"),sQuery(id+"F0.wireOp",EDGE,"E11.17.3"),sQuery(id+"F0.wireOp",EDGE,"E11.17.4"),sQuery(id+"F0.wireOp",EDGE,"E11.17.6"),sQuery(id+"F0.wireOp",EDGE,"E11.17.7"),sQuery(id+"F0.wireOp",EDGE,"E11.17.8"),sQuery(id+"F0.wireOp",EDGE,"E11.17.9"),sQuery(id+"F0.wireOp",EDGE,"E11.17.10"),sQuery(id+"F0.wireOp",EDGE,"E11.17.11"),sQuery(id+"F0.wireOp",EDGE,"E11.17.12"),sQuery(id+"F0.wireOp",EDGE,"E11.18.2"),sQuery(id+"F0.wireOp",EDGE,"E11.18.3"),sQuery(id+"F0.wireOp",EDGE,"E11.18.4"),sQuery(id+"F0.wireOp",EDGE,"E11.18.6"),sQuery(id+"F0.wireOp",EDGE,"E11.18.7"),sQuery(id+"F0.wireOp",EDGE,"E11.18.8"),sQuery(id+"F0.wireOp",EDGE,"E11.18.9"),sQuery(id+"F0.wireOp",EDGE,"E11.18.10"),sQuery(id+"F0.wireOp",EDGE,"E11.18.11"),sQuery(id+"F0.wireOp",EDGE,"E11.18.12"),sQuery(id+"F0.wireOp",EDGE,"E11.19.2"),sQuery(id+"F0.wireOp",EDGE,"E11.19.3"),sQuery(id+"F0.wireOp",EDGE,"E11.19.4"),sQuery(id+"F0.wireOp",EDGE,"E11.19.6"),sQuery(id+"F0.wireOp",EDGE,"E11.19.7"),sQuery(id+"F0.wireOp",EDGE,"E11.19.8"),sQuery(id+"F0.wireOp",EDGE,"E11.19.9"),sQuery(id+"F0.wireOp",EDGE,"E11.19.10"),sQuery(id+"F0.wireOp",EDGE,"E11.19.11"),sQuery(id+"F0.wireOp",EDGE,"E11.19.12"),sQuery(id+"F0.wireOp",EDGE,"E11.20.2"),sQuery(id+"F0.wireOp",EDGE,"E11.20.3"),sQuery(id+"F0.wireOp",EDGE,"E11.20.4"),sQuery(id+"F0.wireOp",EDGE,"E11.20.6"),sQuery(id+"F0.wireOp",EDGE,"E11.20.7"),sQuery(id+"F0.wireOp",EDGE,"E11.20.8"),sQuery(id+"F0.wireOp",EDGE,"E11.20.9"),sQuery(id+"F0.wireOp",EDGE,"E11.20.10"),sQuery(id+"F0.wireOp",EDGE,"E11.20.11"),sQuery(id+"F0.wireOp",EDGE,"E11.20.12"),sQuery(id+"F0.wireOp",EDGE,"E11.21.2"),sQuery(id+"F0.wireOp",EDGE,"E11.21.3"),sQuery(id+"F0.wireOp",EDGE,"E11.21.4"),sQuery(id+"F0.wireOp",EDGE,"E11.21.6"),sQuery(id+"F0.wireOp",EDGE,"E11.21.7"),sQuery(id+"F0.wireOp",EDGE,"E11.21.8"),sQuery(id+"F0.wireOp",EDGE,"E11.21.9"),sQuery(id+"F0.wireOp",EDGE,"E11.21.10"),sQuery(id+"F0.wireOp",EDGE,"E11.21.11"),sQuery(id+"F0.wireOp",EDGE,"E11.21.12"),sQuery(id+"F0.wireOp",EDGE,"E11.22.2"),sQuery(id+"F0.wireOp",EDGE,"E11.22.3"),sQuery(id+"F0.wireOp",EDGE,"E11.22.4"),sQuery(id+"F0.wireOp",EDGE,"E11.22.6"),sQuery(id+"F0.wireOp",EDGE,"E11.22.7"),sQuery(id+"F0.wireOp",EDGE,"E11.22.8"),sQuery(id+"F0.wireOp",EDGE,"E11.22.9"),sQuery(id+"F0.wireOp",EDGE,"E11.22.10"),sQuery(id+"F0.wireOp",EDGE,"E11.22.11"),sQuery(id+"F0.wireOp",EDGE,"E11.22.12"),sQuery(id+"F0.wireOp",EDGE,"E11.23.2"),sQuery(id+"F0.wireOp",EDGE,"E11.23.3"),sQuery(id+"F0.wireOp",EDGE,"E11.23.4"),sQuery(id+"F0.wireOp",EDGE,"E11.23.6"),sQuery(id+"F0.wireOp",EDGE,"E11.23.7"),sQuery(id+"F0.wireOp",EDGE,"E11.23.8"),sQuery(id+"F0.wireOp",EDGE,"E11.23.9"),sQuery(id+"F0.wireOp",EDGE,"E11.23.10"),sQuery(id+"F0.wireOp",EDGE,"E11.23.11"),sQuery(id+"F0.wireOp",EDGE,"E11.23.12"),sQuery(id+"F0.wireOp",EDGE,"E12.trimOffspring"),sQuery(id+"F0.wireOp",EDGE,"E13.trimOffspring"),sQuery(id+"F0.wireOp",EDGE,"E14.trimOffspring"),sQuery(id+"F0.wireOp",EDGE,"E15.trimOffspring"),sQuery(id+"F0.wireOp",EDGE,"E16.trimOffspring"),sQuery(id+"F0.wireOp",EDGE,"E17.trimOffspring"),sQuery(id+"F0.wireOp",EDGE,"E18.trimOffspring"),sQuery(id+"F0.wireOp",EDGE,"E19.trimOffspring"),sQuery(id+"F0.wireOp",EDGE,"E20.trimOffspring"),sQuery(id+"F0.wireOp",EDGE,"E21.trimOffspring"),sQuery(id+"F0.wireOp",EDGE,"E22.trimOffspring"),sQuery(id+"F0.wireOp",EDGE,"E23.trimOffspring"),sQuery(id+"F0.wireOp",EDGE,"E24.trimOffspring"),sQuery(id+"F0.wireOp",EDGE,"E25.trimOffspring"),sQuery(id+"F0.wireOp",EDGE,"E26.trimOffspring"),sQuery(id+"F0.wireOp",EDGE,"E27.trimOffspring"),sQuery(id+"F0.wireOp",EDGE,"E28.trimOffspring"),sQuery(id+"F0.wireOp",EDGE,"E29.trimOffspring"),sQuery(id+"F0.wireOp",EDGE,"E30.trimOffspring"),sQuery(id+"F0.wireOp",EDGE,"E31.trimOffspring"),sQuery(id+"F0.wireOp",EDGE,"E32.trimOffspring"),sQuery(id+"F0.wireOp",EDGE,"E33.trimOffspring")])]});
            hole(context, id + "F5", {"style" : HoleStyle.SIMPLE, "endStyle" : HoleEndStyle.THROUGH, "holeDiameter" : 6.35 * mm, "locations" : qUnion([Q0]), "scope" : qUnion([Q1]), "isTappedThrough" : true});
        }
    });
